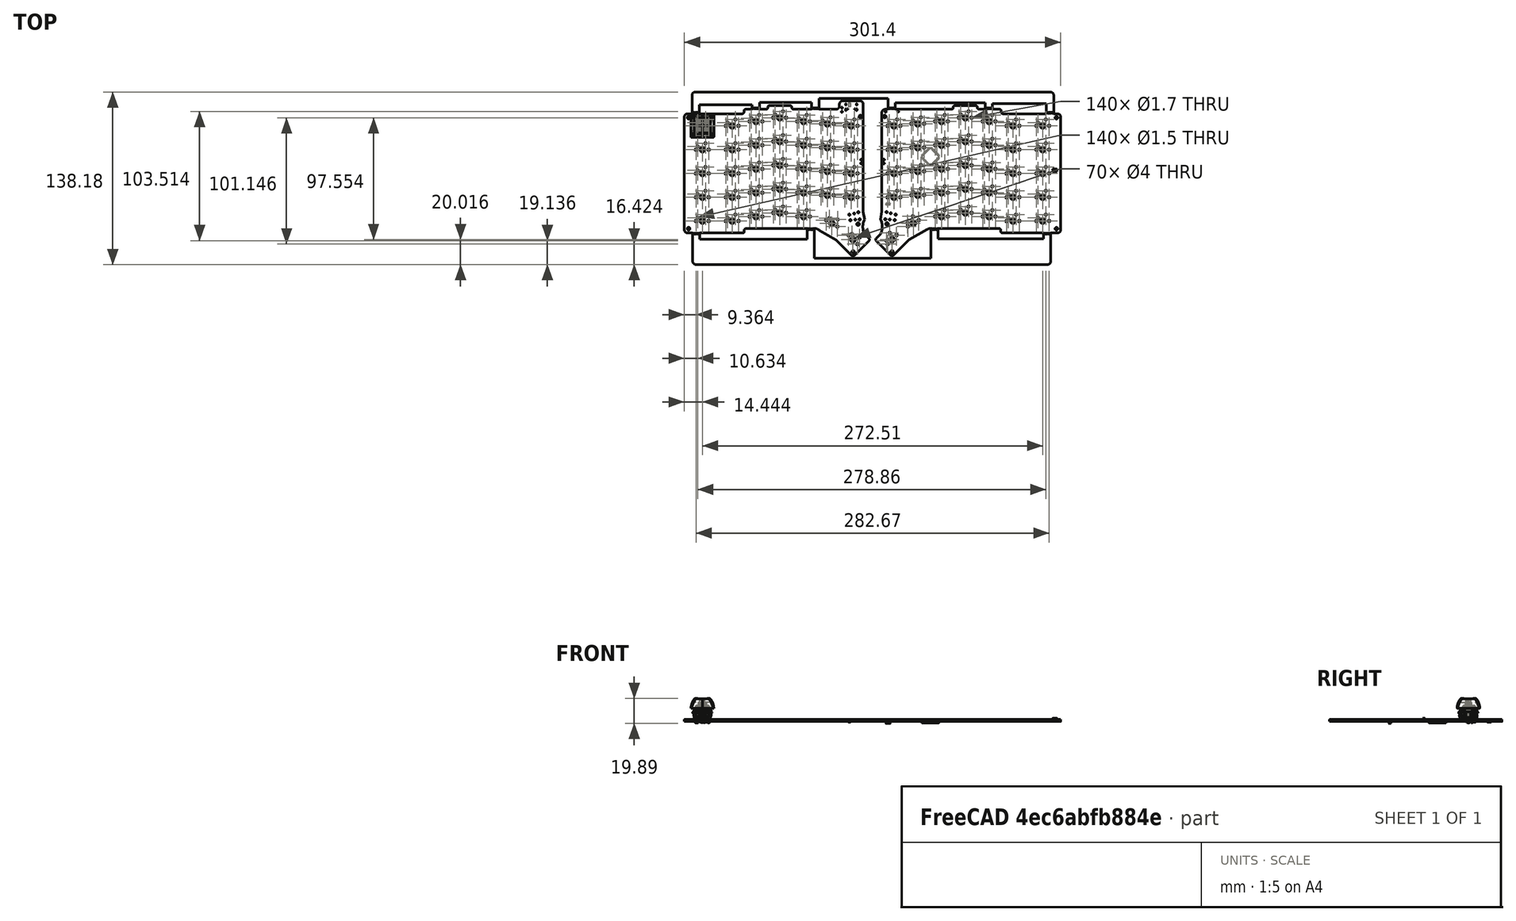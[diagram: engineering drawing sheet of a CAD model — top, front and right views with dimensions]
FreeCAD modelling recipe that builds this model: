
FCSTD DOCUMENT  (FreeCAD 0.19R24291 (Git))
Label: wholeModel
License: All rights reserved
LicenseURL: http://en.wikipedia.org/wiki/All_rights_reserved
objects: App::Link×226, Part::Feature×7, App::Part×5, PartDesign::CoordinateSystem×1, Sketcher::SketchObject×1
note: 9 computed .brp shape members not serialized (recipe doc carries the construction recipe); baked Part::Feature solids carry a one-line shape summary decoded from their .brp

FEATURE [PartDesign::CoordinateSystem] Local_CS_2136
  AttacherType = Attacher::AttachEngine3D
FEATURE [Part::Feature] Pcb_2136
  shape: bbox 301.4 x 138.2 x 1.6 mm, 613 faces (baked)
FEATURE [Sketcher::SketchObject] PCB_Sketch_2136
  FullyConstrained = false
  sketch-geometry (205):
    g0: LineSegment StartX=297.923 StartY=-40.503 StartZ=0 EndX=294.907 EndY=-40.503 EndZ=0
    g1: LineSegment StartX=240.043 StartY=-36.947 StartZ=0 EndX=235.058 EndY=-36.947 EndZ=0
    g2: LineSegment StartX=162.192 StartY=-36.947 StartZ=0 EndX=160.001 EndY=-36.947 EndZ=0
    g3: LineSegment StartX=53.48 StartY=-36.947 StartZ=0 EndX=48.2095 EndY=-36.947 EndZ=0
    g4: LineSegment StartX=5.347 StartY=-40.503 StartZ=0 EndX=1.8545 EndY=-40.503 EndZ=0
    g5: LineSegment StartX=292.621 StartY=-136.007 StartZ=0 EndX=297.923 EndY=-136.007 EndZ=0
    g6: LineSegment StartX=196.609 StartY=-132.451 StartZ=0 EndX=195.688 EndY=-132.449 EndZ=0
    g7: LineSegment StartX=103.264 StartY=-132.451 StartZ=0 EndX=104.217 EndY=-132.449 EndZ=0
    g8: LineSegment StartX=202.451 StartY=-140.579 StartZ=0 EndX=286.779 EndY=-140.579 EndZ=0
    g9: LineSegment StartX=292.621 StartY=-156.2 StartZ=0 EndX=292.62 EndY=-158.608 EndZ=0
    g10: LineSegment StartX=134.252 StartY=-156.2 StartZ=0 EndX=196.609 EndY=-156.2 EndZ=0
    g11: LineSegment StartX=292.621 StartY=-137.277 StartZ=0 EndX=292.621 EndY=-156.2 EndZ=0
    g12: LineSegment StartX=286.779 StartY=-137.277 StartZ=0 EndX=286.779 EndY=-140.579 EndZ=0
    g13: LineSegment StartX=202.451 StartY=-133.721 StartZ=0 EndX=202.451 EndY=-140.579 EndZ=0
    g14: LineSegment StartX=196.609 StartY=-133.721 StartZ=0 EndX=196.609 EndY=-156.2 EndZ=0
    g15: LineSegment StartX=97.422 StartY=-140.833 StartZ=0 EndX=11.57 EndY=-140.833 EndZ=0
    g16: LineSegment StartX=97.422 StartY=-133.721 StartZ=0 EndX=97.422 EndY=-140.833 EndZ=0
    g17: LineSegment StartX=103.264 StartY=-133.721 StartZ=0 EndX=103.264 EndY=-156.2 EndZ=0
    g18: LineSegment StartX=5.855 StartY=-156.2 StartZ=0 EndX=5.8574 EndY=-158.61 EndZ=0
    g19: LineSegment StartX=5.855 StartY=-137.277 StartZ=0 EndX=5.855 EndY=-156.2 EndZ=0
    g20: LineSegment StartX=11.57 StartY=-140.833 StartZ=0 EndX=11.57 EndY=-137.277 EndZ=0
    g21: LineSegment StartX=134.252 StartY=-156.2 StartZ=0 EndX=103.264 EndY=-156.2 EndZ=0
    g22: LineSegment StartX=289.953 StartY=-161.275 StartZ=0 EndX=8.5244 EndY=-161.277 EndZ=0
    g23: LineSegment StartX=294.904 StartY=-25.7686 StartZ=0 EndX=294.907 EndY=-28.184 EndZ=0
    g24: LineSegment StartX=108.217 StartY=-23.104 StartZ=0 EndX=292.237 EndY=-23.1016 EndZ=0
    g25: LineSegment StartX=294.907 StartY=-39.233 StartZ=0 EndX=294.907 EndY=-28.184 EndZ=0
    g26: LineSegment StartX=289.065 StartY=-32.502 StartZ=0 EndX=289.065 EndY=-39.233 EndZ=0
    g27: LineSegment StartX=245.885 StartY=-32.502 StartZ=0 EndX=289.065 EndY=-32.502 EndZ=0
    g28: LineSegment StartX=245.885 StartY=-35.677 StartZ=0 EndX=245.885 EndY=-32.502 EndZ=0
    g29: LineSegment StartX=240.043 StartY=-31.613 StartZ=0 EndX=240.043 EndY=-35.677 EndZ=0
    g30: LineSegment StartX=168.034 StartY=-31.613 StartZ=0 EndX=240.043 EndY=-31.613 EndZ=0
    g31: LineSegment StartX=168.034 StartY=-35.55 StartZ=0 EndX=168.034 EndY=-31.613 EndZ=0
    g32: LineSegment StartX=162.192 StartY=-28.184 StartZ=0 EndX=162.192 EndY=-35.677 EndZ=0
    g33: LineSegment StartX=126.505 StartY=-28.184 StartZ=0 EndX=162.192 EndY=-28.184 EndZ=0
    g34: LineSegment StartX=5.347 StartY=-25.771 StartZ=0 EndX=5.347 EndY=-28.184 EndZ=0
    g35: LineSegment StartX=106.947 StartY=-23.104 StartZ=0 EndX=8.014 EndY=-23.104 EndZ=0
    g36: LineSegment StartX=5.347 StartY=-28.311 StartZ=0 EndX=5.347 EndY=-28.184 EndZ=0
    g37: LineSegment StartX=5.347 StartY=-39.233 StartZ=0 EndX=5.347 EndY=-28.311 EndZ=0
    g38: LineSegment StartX=11.189 StartY=-33.391 StartZ=0 EndX=11.189 EndY=-39.233 EndZ=0
    g39: LineSegment StartX=53.48 StartY=-33.391 StartZ=0 EndX=11.189 EndY=-33.391 EndZ=0
    g40: LineSegment StartX=53.48 StartY=-35.677 StartZ=0 EndX=53.48 EndY=-33.391 EndZ=0
    g41: LineSegment StartX=59.322 StartY=-31.486 StartZ=0 EndX=59.322 EndY=-35.677 EndZ=0
    g42: LineSegment StartX=101.105 StartY=-31.486 StartZ=0 EndX=59.322 EndY=-31.486 EndZ=0
    g43: LineSegment StartX=101.105 StartY=-35.677 StartZ=0 EndX=101.105 EndY=-31.486 EndZ=0
    g44: LineSegment StartX=106.947 StartY=-23.104 StartZ=0 EndX=108.217 EndY=-23.104 EndZ=0
    g45: LineSegment StartX=106.947 StartY=-28.184 StartZ=0 EndX=126.505 EndY=-28.184 EndZ=0
    g46: LineSegment StartX=106.947 StartY=-35.677 StartZ=0 EndX=106.947 EndY=-28.184 EndZ=0
    g47: LineSegment StartX=5.347 StartY=-39.233 StartZ=0 EndX=5.347 EndY=-40.503 EndZ=0
    g48: LineSegment StartX=11.189 StartY=-39.233 StartZ=0 EndX=11.189 EndY=-40.503 EndZ=0
    g49: LineSegment StartX=53.48 StartY=-35.677 StartZ=0 EndX=53.48 EndY=-36.947 EndZ=0
    g50: LineSegment StartX=59.322 StartY=-35.677 StartZ=0 EndX=59.322 EndY=-36.947 EndZ=0
    g51: LineSegment StartX=101.105 StartY=-35.677 StartZ=0 EndX=101.105 EndY=-36.947 EndZ=0
    g52: LineSegment StartX=106.947 StartY=-35.677 StartZ=0 EndX=106.947 EndY=-36.947 EndZ=0
    g53: LineSegment StartX=162.192 StartY=-35.677 StartZ=0 EndX=162.192 EndY=-36.947 EndZ=0
    g54: LineSegment StartX=168.034 StartY=-35.55 StartZ=0 EndX=168.034 EndY=-36.947 EndZ=0
    g55: LineSegment StartX=240.043 StartY=-35.677 StartZ=0 EndX=240.043 EndY=-36.947 EndZ=0
    g56: LineSegment StartX=245.885 StartY=-35.677 StartZ=0 EndX=245.885 EndY=-36.947 EndZ=0
    g57: LineSegment StartX=289.065 StartY=-39.233 StartZ=0 EndX=289.065 EndY=-40.503 EndZ=0
    g58: LineSegment StartX=294.907 StartY=-39.233 StartZ=0 EndX=294.907 EndY=-40.503 EndZ=0
    g59: LineSegment StartX=286.779 StartY=-136.007 StartZ=0 EndX=286.779 EndY=-137.277 EndZ=0
    g60: LineSegment StartX=292.621 StartY=-136.007 StartZ=0 EndX=292.621 EndY=-137.277 EndZ=0
    g61: LineSegment StartX=196.609 StartY=-132.451 StartZ=0 EndX=196.609 EndY=-133.721 EndZ=0
    g62: LineSegment StartX=202.451 StartY=-132.451 StartZ=0 EndX=202.451 EndY=-133.721 EndZ=0
    g63: LineSegment StartX=97.422 StartY=-132.451 StartZ=0 EndX=97.422 EndY=-133.721 EndZ=0
    g64: LineSegment StartX=103.264 StartY=-132.451 StartZ=0 EndX=103.264 EndY=-133.721 EndZ=0
    g65: LineSegment StartX=11.57 StartY=-136.007 StartZ=0 EndX=11.57 EndY=-137.277 EndZ=0
    g66: LineSegment StartX=11.57 StartY=-136.007 StartZ=0 EndX=45.9235 EndY=-136.007 EndZ=0
    g67: LineSegment StartX=5.855 StartY=-136.007 StartZ=0 EndX=5.855 EndY=-137.277 EndZ=0
    g68: LineSegment StartX=1.8545 StartY=-136.007 StartZ=0 EndX=5.855 EndY=-136.007 EndZ=0
    g69: LineSegment StartX=193.656 StartY=-133.086 StartZ=0 EndX=179.178 EndY=-141.341 EndZ=0
    g70: LineSegment StartX=214.484 StartY=-35.677 StartZ=0 EndX=214.484 EndY=-35.296 EndZ=0
    g71: LineSegment StartX=147.016 StartY=-140.198 StartZ=0 EndX=143.587 EndY=-136.769 EndZ=0
    g72: LineSegment StartX=120.6 StartY=-141.468 StartZ=0 EndX=133.173 EndY=-154.041 EndZ=0
    g73: LineSegment StartX=106.249 StartY=-133.086 StartZ=0 EndX=106.629 EndY=-133.34 EndZ=0
    g74: LineSegment StartX=107.519 StartY=-133.848 StartZ=0 EndX=120.6 EndY=-141.468 EndZ=0
    g75: LineSegment StartX=107.519 StartY=-133.848 StartZ=0 EndX=106.629 EndY=-133.34 EndZ=0
    g76: LineSegment StartX=120.727 StartY=-36.947 StartZ=0 EndX=106.947 EndY=-36.947 EndZ=0
    g77: LineSegment StartX=123.394 StartY=-34.28 StartZ=0 EndX=123.394 EndY=-32.893 EndZ=0
    g78: LineSegment StartX=139.776 StartY=-30.216 StartZ=0 EndX=126.061 EndY=-30.216 EndZ=0
    g79: LineSegment StartX=142.444 StartY=-38.725 StartZ=0 EndX=142.443 EndY=-32.893 EndZ=0
    g80: LineSegment StartX=85.2935 StartY=-35.677 StartZ=0 EndX=85.2935 EndY=-35.296 EndZ=0
    g81: LineSegment StartX=101.105 StartY=-36.947 StartZ=0 EndX=86.5635 EndY=-36.947 EndZ=0
    g82: LineSegment StartX=84.0235 StartY=-34.026 StartZ=0 EndX=67.2595 EndY=-34.026 EndZ=0
    g83: LineSegment StartX=65.9895 StartY=-35.296 StartZ=0 EndX=65.9895 EndY=-35.677 EndZ=0
    g84: LineSegment StartX=152.762 StartY=-140.198 StartZ=0 EndX=156.191 EndY=-136.769 EndZ=0
    g85: LineSegment StartX=164.446 StartY=-153.914 StartZ=0 EndX=152.762 EndY=-142.23 EndZ=0
    g86: LineSegment StartX=178.924 StartY=-141.468 StartZ=0 EndX=166.478 EndY=-153.914 EndZ=0
    g87: LineSegment StartX=179.178 StartY=-141.341 StartZ=0 EndX=178.924 EndY=-141.468 EndZ=0
    g88: LineSegment StartX=214.738 StartY=-132.451 StartZ=0 EndX=202.451 EndY=-132.451 EndZ=0
    g89: LineSegment StartX=233.534 StartY=-132.451 StartZ=0 EndX=214.738 EndY=-132.451 EndZ=0
    g90: LineSegment StartX=251.314 StartY=-132.451 StartZ=0 EndX=233.534 EndY=-132.451 EndZ=0
    g91: LineSegment StartX=252.584 StartY=-134.737 StartZ=0 EndX=252.584 EndY=-133.721 EndZ=0
    g92: LineSegment StartX=286.779 StartY=-136.007 StartZ=0 EndX=253.854 EndY=-136.007 EndZ=0
    g93: LineSegment StartX=300.59 StartY=-43.17 StartZ=0 EndX=300.59 EndY=-133.34 EndZ=0
    g94: LineSegment StartX=254.108 StartY=-40.503 StartZ=0 EndX=289.065 EndY=-40.503 EndZ=0
    g95: LineSegment StartX=252.838 StartY=-38.217 StartZ=0 EndX=252.838 EndY=-39.233 EndZ=0
    g96: LineSegment StartX=245.885 StartY=-36.947 StartZ=0 EndX=251.568 EndY=-36.947 EndZ=0
    g97: LineSegment StartX=233.788 StartY=-35.296 StartZ=0 EndX=233.788 EndY=-35.677 EndZ=0
    g98: LineSegment StartX=157.334 StartY=-39.614 StartZ=0 EndX=157.334 EndY=-40.503 EndZ=0
    g99: LineSegment StartX=213.214 StartY=-36.947 StartZ=0 EndX=168.034 EndY=-36.947 EndZ=0
    g100: LineSegment StartX=232.518 StartY=-34.026 StartZ=0 EndX=215.754 EndY=-34.026 EndZ=0
    g101: LineSegment StartX=157.334 StartY=-116.068 StartZ=0 EndX=157.334 EndY=-40.503 EndZ=0
    g102: LineSegment StartX=157.334 StartY=-118.862 StartZ=0 EndX=156.191 EndY=-125.085 EndZ=0
    g103: LineSegment StartX=157.334 StartY=-116.957 StartZ=0 EndX=157.334 EndY=-118.862 EndZ=0
    g104: LineSegment StartX=157.334 StartY=-116.068 StartZ=0 EndX=157.334 EndY=-116.957 EndZ=0
    g105: LineSegment StartX=142.444 StartY=-116.195 StartZ=0 EndX=142.444 EndY=-41.138 EndZ=0
    g106: LineSegment StartX=142.444 StartY=-118.989 StartZ=0 EndX=143.587 EndY=-125.085 EndZ=0
    g107: LineSegment StartX=142.444 StartY=-116.957 StartZ=0 EndX=142.444 EndY=-118.989 EndZ=0
    g108: LineSegment StartX=142.444 StartY=-116.195 StartZ=0 EndX=142.444 EndY=-116.957 EndZ=0
    g109: LineSegment StartX=135.204 StartY=-154.041 StartZ=0 EndX=147.016 EndY=-142.23 EndZ=0
    g110: LineSegment StartX=85.0395 StartY=-132.451 StartZ=0 EndX=97.422 EndY=-132.451 EndZ=0
    g111: LineSegment StartX=66.2435 StartY=-132.451 StartZ=0 EndX=85.0395 EndY=-132.451 EndZ=0
    g112: LineSegment StartX=48.4635 StartY=-132.451 StartZ=0 EndX=66.2435 EndY=-132.451 EndZ=0
    g113: LineSegment StartX=47.1935 StartY=-134.737 StartZ=0 EndX=47.1935 EndY=-133.721 EndZ=0
    g114: LineSegment StartX=-0.8125 StartY=-43.17 StartZ=0 EndX=-0.8125 EndY=-133.34 EndZ=0
    g115: LineSegment StartX=45.6695 StartY=-40.503 StartZ=0 EndX=11.189 EndY=-40.503 EndZ=0
    g116: LineSegment StartX=46.9395 StartY=-38.217 StartZ=0 EndX=46.9395 EndY=-39.233 EndZ=0
    g117: LineSegment StartX=64.7195 StartY=-36.947 StartZ=0 EndX=59.322 EndY=-36.947 EndZ=0
    g118: LineSegment StartX=142.444 StartY=-41.138 StartZ=0 EndX=142.444 EndY=-38.725 EndZ=0
    g119: ArcOfCircle CenterX=289.953 CenterY=-158.608 CenterZ=0 NormalX=0 NormalY=0 NormalZ=1 AngleXU=0 Radius=2.667 StartAngle=4.71239 EndAngle=6.28319
    g120: ArcOfCircle CenterX=8.5244 CenterY=-158.61 CenterZ=0 NormalX=0 NormalY=0 NormalZ=1 AngleXU=0 Radius=2.667 StartAngle=3.14159 EndAngle=4.71239
    g121: ArcOfCircle CenterX=292.237 CenterY=-25.7686 CenterZ=0 NormalX=0 NormalY=0 NormalZ=1 AngleXU=0 Radius=2.667 StartAngle=0 EndAngle=1.5708
    g122: ArcOfCircle CenterX=8.014 CenterY=-25.771 CenterZ=0 NormalX=0 NormalY=0 NormalZ=1 AngleXU=0 Radius=2.667 StartAngle=1.5708 EndAngle=3.14159
    g123: ArcOfCircle CenterX=154.254 CenterY=-130.927 CenterZ=0 NormalX=0 NormalY=0 NormalZ=1 AngleXU=0 Radius=12.1629 StartAngle=2.64058 EndAngle=3.64261
    g124: ArcOfCircle CenterX=145.523 CenterY=-130.927 CenterZ=0 NormalX=0 NormalY=0 NormalZ=1 AngleXU=0 Radius=12.1629 StartAngle=5.78217 EndAngle=6.7842
    g125: ArcOfCircle CenterX=195.688 CenterY=-136.007 CenterZ=0 NormalX=0 NormalY=0 NormalZ=1 AngleXU=0 Radius=3.55827 StartAngle=1.5708 EndAngle=2.1786
    g126: ArcOfCircle CenterX=153.778 CenterY=-141.214 CenterZ=0 NormalX=0 NormalY=0 NormalZ=1 AngleXU=0 Radius=1.43684 StartAngle=2.35619 EndAngle=3.92699
    g127: ArcOfCircle CenterX=297.923 CenterY=-43.17 CenterZ=0 NormalX=0 NormalY=0 NormalZ=1 AngleXU=0 Radius=2.667 StartAngle=0 EndAngle=1.5708
    g128: ArcOfCircle CenterX=297.923 CenterY=-133.34 CenterZ=0 NormalX=0 NormalY=0 NormalZ=1 AngleXU=0 Radius=2.667 StartAngle=4.71239 EndAngle=6.28319
    g129: ArcOfCircle CenterX=251.314 CenterY=-133.721 CenterZ=0 NormalX=0 NormalY=0 NormalZ=1 AngleXU=0 Radius=1.27 StartAngle=0 EndAngle=1.5708
    g130: ArcOfCircle CenterX=253.854 CenterY=-134.737 CenterZ=0 NormalX=0 NormalY=0 NormalZ=1 AngleXU=0 Radius=1.27 StartAngle=3.14159 EndAngle=4.71239
    g131: ArcOfCircle CenterX=254.108 CenterY=-39.233 CenterZ=0 NormalX=0 NormalY=0 NormalZ=1 AngleXU=0 Radius=1.27 StartAngle=3.14159 EndAngle=4.71239
    g132: ArcOfCircle CenterX=251.568 CenterY=-38.217 CenterZ=0 NormalX=0 NormalY=0 NormalZ=1 AngleXU=0 Radius=1.27 StartAngle=0 EndAngle=1.5708
    g133: ArcOfCircle CenterX=235.058 CenterY=-35.677 CenterZ=0 NormalX=0 NormalY=0 NormalZ=1 AngleXU=0 Radius=1.27 StartAngle=3.14159 EndAngle=4.71239
    g134: ArcOfCircle CenterX=232.518 CenterY=-35.296 CenterZ=0 NormalX=0 NormalY=0 NormalZ=1 AngleXU=0 Radius=1.27 StartAngle=0 EndAngle=1.5708
    g135: ArcOfCircle CenterX=215.754 CenterY=-35.296 CenterZ=0 NormalX=0 NormalY=0 NormalZ=1 AngleXU=0 Radius=1.27 StartAngle=1.5708 EndAngle=3.14159
    g136: ArcOfCircle CenterX=213.214 CenterY=-35.677 CenterZ=0 NormalX=0 NormalY=0 NormalZ=1 AngleXU=0 Radius=1.27 StartAngle=4.71239 EndAngle=6.28319
    g137: ArcOfCircle CenterX=146 CenterY=-141.214 CenterZ=0 NormalX=0 NormalY=0 NormalZ=1 AngleXU=0 Radius=1.43684 StartAngle=5.49779 EndAngle=7.06858
    g138: ArcOfCircle CenterX=165.462 CenterY=-152.898 CenterZ=0 NormalX=0 NormalY=0 NormalZ=1 AngleXU=0 Radius=1.43684 StartAngle=3.92699 EndAngle=5.49779
    g139: ArcOfCircle CenterX=134.189 CenterY=-153.025 CenterZ=0 NormalX=0 NormalY=0 NormalZ=1 AngleXU=0 Radius=1.43684 StartAngle=3.92699 EndAngle=5.49779
    g140: ArcOfCircle CenterX=104.217 CenterY=-136.007 CenterZ=0 NormalX=0 NormalY=0 NormalZ=1 AngleXU=0 Radius=3.55827 StartAngle=0.962994 EndAngle=1.5708
    g141: ArcOfCircle CenterX=1.8545 CenterY=-133.34 CenterZ=0 NormalX=0 NormalY=0 NormalZ=1 AngleXU=0 Radius=2.667 StartAngle=3.14159 EndAngle=4.71239
    g142: ArcOfCircle CenterX=1.8545 CenterY=-43.17 CenterZ=0 NormalX=0 NormalY=0 NormalZ=1 AngleXU=0 Radius=2.667 StartAngle=1.5708 EndAngle=3.14159
    g143: ArcOfCircle CenterX=48.4635 CenterY=-133.721 CenterZ=0 NormalX=0 NormalY=0 NormalZ=1 AngleXU=0 Radius=1.27 StartAngle=1.5708 EndAngle=3.14159
    g144: ArcOfCircle CenterX=45.9235 CenterY=-134.737 CenterZ=0 NormalX=0 NormalY=0 NormalZ=1 AngleXU=0 Radius=1.27 StartAngle=4.71239 EndAngle=6.28319
    g145: ArcOfCircle CenterX=45.6695 CenterY=-39.233 CenterZ=0 NormalX=0 NormalY=0 NormalZ=1 AngleXU=0 Radius=1.27 StartAngle=4.71239 EndAngle=6.28319
    g146: ArcOfCircle CenterX=48.2095 CenterY=-38.217 CenterZ=0 NormalX=0 NormalY=0 NormalZ=1 AngleXU=0 Radius=1.27 StartAngle=1.5708 EndAngle=3.14159
    g147: ArcOfCircle CenterX=64.7195 CenterY=-35.677 CenterZ=0 NormalX=0 NormalY=0 NormalZ=1 AngleXU=0 Radius=1.27 StartAngle=4.71239 EndAngle=6.28319
    g148: ArcOfCircle CenterX=86.5635 CenterY=-35.677 CenterZ=0 NormalX=0 NormalY=0 NormalZ=1 AngleXU=0 Radius=1.27 StartAngle=3.14159 EndAngle=4.71239
    g149: ArcOfCircle CenterX=67.2595 CenterY=-35.296 CenterZ=0 NormalX=0 NormalY=0 NormalZ=1 AngleXU=0 Radius=1.27 StartAngle=1.5708 EndAngle=3.14159
    g150: ArcOfCircle CenterX=84.0235 CenterY=-35.296 CenterZ=0 NormalX=0 NormalY=0 NormalZ=1 AngleXU=0 Radius=1.27 StartAngle=0 EndAngle=1.5708
    g151: ArcOfCircle CenterX=120.727 CenterY=-34.28 CenterZ=0 NormalX=0 NormalY=0 NormalZ=1 AngleXU=0 Radius=2.667 StartAngle=4.71239 EndAngle=6.28319
    g152: ArcOfCircle CenterX=160.001 CenterY=-39.614 CenterZ=0 NormalX=0 NormalY=0 NormalZ=1 AngleXU=0 Radius=2.667 StartAngle=1.5708 EndAngle=3.14159
    g153: ArcOfCircle CenterX=126.06 CenterY=-32.883 CenterZ=0 NormalX=0 NormalY=0 NormalZ=1 AngleXU=0 Radius=2.66702 StartAngle=1.5708 EndAngle=3.14534
    g154: ArcOfCircle CenterX=139.776 CenterY=-32.883 CenterZ=0 NormalX=0 NormalY=0 NormalZ=1 AngleXU=0 Radius=2.66702 StartAngle=6.27944 EndAngle=7.85398
    g155: Circle CenterX=10.554 CenterY=-39.741 CenterZ=0 NormalX=0 NormalY=0 NormalZ=1 AngleXU=0 Radius=0.457905
    g156: Circle CenterX=5.982 CenterY=-39.741 CenterZ=0 NormalX=0 NormalY=0 NormalZ=1 AngleXU=0 Radius=0.457905
    g157: Circle CenterX=9.411 CenterY=-39.741 CenterZ=0 NormalX=0 NormalY=0 NormalZ=1 AngleXU=0 Radius=0.457905
    g158: Circle CenterX=7.125 CenterY=-39.741 CenterZ=0 NormalX=0 NormalY=0 NormalZ=1 AngleXU=0 Radius=0.457905
    g159: Circle CenterX=8.268 CenterY=-39.741 CenterZ=0 NormalX=0 NormalY=0 NormalZ=1 AngleXU=0 Radius=0.457905
    g160: Circle CenterX=58.687 CenterY=-36.185 CenterZ=0 NormalX=0 NormalY=0 NormalZ=1 AngleXU=0 Radius=0.457905
    g161: Circle CenterX=54.115 CenterY=-36.185 CenterZ=0 NormalX=0 NormalY=0 NormalZ=1 AngleXU=0 Radius=0.457905
    g162: Circle CenterX=57.544 CenterY=-36.185 CenterZ=0 NormalX=0 NormalY=0 NormalZ=1 AngleXU=0 Radius=0.457905
    g163: Circle CenterX=55.258 CenterY=-36.185 CenterZ=0 NormalX=0 NormalY=0 NormalZ=1 AngleXU=0 Radius=0.457905
    g164: Circle CenterX=56.401 CenterY=-36.185 CenterZ=0 NormalX=0 NormalY=0 NormalZ=1 AngleXU=0 Radius=0.457905
    g165: Circle CenterX=106.312 CenterY=-36.185 CenterZ=0 NormalX=0 NormalY=0 NormalZ=1 AngleXU=0 Radius=0.457905
    g166: Circle CenterX=101.74 CenterY=-36.185 CenterZ=0 NormalX=0 NormalY=0 NormalZ=1 AngleXU=0 Radius=0.457905
    g167: Circle CenterX=105.169 CenterY=-36.185 CenterZ=0 NormalX=0 NormalY=0 NormalZ=1 AngleXU=0 Radius=0.457905
    g168: Circle CenterX=102.883 CenterY=-36.185 CenterZ=0 NormalX=0 NormalY=0 NormalZ=1 AngleXU=0 Radius=0.457905
    g169: Circle CenterX=104.026 CenterY=-36.185 CenterZ=0 NormalX=0 NormalY=0 NormalZ=1 AngleXU=0 Radius=0.457905
    g170: Circle CenterX=167.399 CenterY=-36.185 CenterZ=0 NormalX=0 NormalY=0 NormalZ=1 AngleXU=0 Radius=0.457905
    g171: Circle CenterX=162.827 CenterY=-36.185 CenterZ=0 NormalX=0 NormalY=0 NormalZ=1 AngleXU=0 Radius=0.457905
    g172: Circle CenterX=166.256 CenterY=-36.185 CenterZ=0 NormalX=0 NormalY=0 NormalZ=1 AngleXU=0 Radius=0.457905
    g173: Circle CenterX=163.97 CenterY=-36.185 CenterZ=0 NormalX=0 NormalY=0 NormalZ=1 AngleXU=0 Radius=0.457905
    g174: Circle CenterX=165.113 CenterY=-36.185 CenterZ=0 NormalX=0 NormalY=0 NormalZ=1 AngleXU=0 Radius=0.457905
    g175: Circle CenterX=245.25 CenterY=-36.185 CenterZ=0 NormalX=0 NormalY=0 NormalZ=1 AngleXU=0 Radius=0.457905
    g176: Circle CenterX=240.678 CenterY=-36.185 CenterZ=0 NormalX=0 NormalY=0 NormalZ=1 AngleXU=0 Radius=0.457905
    g177: Circle CenterX=244.107 CenterY=-36.185 CenterZ=0 NormalX=0 NormalY=0 NormalZ=1 AngleXU=0 Radius=0.457905
    g178: Circle CenterX=241.821 CenterY=-36.185 CenterZ=0 NormalX=0 NormalY=0 NormalZ=1 AngleXU=0 Radius=0.457905
    g179: Circle CenterX=242.964 CenterY=-36.185 CenterZ=0 NormalX=0 NormalY=0 NormalZ=1 AngleXU=0 Radius=0.457905
    g180: Circle CenterX=294.272 CenterY=-39.741 CenterZ=0 NormalX=0 NormalY=0 NormalZ=1 AngleXU=0 Radius=0.457905
    g181: Circle CenterX=289.7 CenterY=-39.741 CenterZ=0 NormalX=0 NormalY=0 NormalZ=1 AngleXU=0 Radius=0.457905
    g182: Circle CenterX=293.129 CenterY=-39.741 CenterZ=0 NormalX=0 NormalY=0 NormalZ=1 AngleXU=0 Radius=0.457905
    g183: Circle CenterX=290.843 CenterY=-39.741 CenterZ=0 NormalX=0 NormalY=0 NormalZ=1 AngleXU=0 Radius=0.457905
    g184: Circle CenterX=291.986 CenterY=-39.741 CenterZ=0 NormalX=0 NormalY=0 NormalZ=1 AngleXU=0 Radius=0.457905
    g185: Circle CenterX=291.986 CenterY=-136.515 CenterZ=0 NormalX=0 NormalY=0 NormalZ=1 AngleXU=0 Radius=0.457905
    g186: Circle CenterX=287.414 CenterY=-136.515 CenterZ=0 NormalX=0 NormalY=0 NormalZ=1 AngleXU=0 Radius=0.457905
    g187: Circle CenterX=290.843 CenterY=-136.515 CenterZ=0 NormalX=0 NormalY=0 NormalZ=1 AngleXU=0 Radius=0.457905
    g188: Circle CenterX=288.557 CenterY=-136.515 CenterZ=0 NormalX=0 NormalY=0 NormalZ=1 AngleXU=0 Radius=0.457905
    g189: Circle CenterX=289.7 CenterY=-136.515 CenterZ=0 NormalX=0 NormalY=0 NormalZ=1 AngleXU=0 Radius=0.457905
    g190: Circle CenterX=201.816 CenterY=-132.959 CenterZ=0 NormalX=0 NormalY=0 NormalZ=1 AngleXU=0 Radius=0.457905
    g191: Circle CenterX=197.244 CenterY=-132.959 CenterZ=0 NormalX=0 NormalY=0 NormalZ=1 AngleXU=0 Radius=0.457905
    g192: Circle CenterX=200.673 CenterY=-132.959 CenterZ=0 NormalX=0 NormalY=0 NormalZ=1 AngleXU=0 Radius=0.457905
    g193: Circle CenterX=198.387 CenterY=-132.959 CenterZ=0 NormalX=0 NormalY=0 NormalZ=1 AngleXU=0 Radius=0.457905
    g194: Circle CenterX=199.53 CenterY=-132.959 CenterZ=0 NormalX=0 NormalY=0 NormalZ=1 AngleXU=0 Radius=0.457905
    g195: Circle CenterX=102.629 CenterY=-132.959 CenterZ=0 NormalX=0 NormalY=0 NormalZ=1 AngleXU=0 Radius=0.457905
    g196: Circle CenterX=98.057 CenterY=-132.959 CenterZ=0 NormalX=0 NormalY=0 NormalZ=1 AngleXU=0 Radius=0.457905
    g197: Circle CenterX=101.486 CenterY=-132.959 CenterZ=0 NormalX=0 NormalY=0 NormalZ=1 AngleXU=0 Radius=0.457905
    g198: Circle CenterX=99.2 CenterY=-132.959 CenterZ=0 NormalX=0 NormalY=0 NormalZ=1 AngleXU=0 Radius=0.457905
    g199: Circle CenterX=100.343 CenterY=-132.959 CenterZ=0 NormalX=0 NormalY=0 NormalZ=1 AngleXU=0 Radius=0.457905
    g200: Circle CenterX=6.43991 CenterY=-136.515 CenterZ=0 NormalX=0 NormalY=0 NormalZ=1 AngleXU=0 Radius=0.457905
    g201: Circle CenterX=11.0119 CenterY=-136.515 CenterZ=0 NormalX=0 NormalY=0 NormalZ=1 AngleXU=0 Radius=0.457905
    g202: Circle CenterX=8.7259 CenterY=-136.515 CenterZ=0 NormalX=0 NormalY=0 NormalZ=1 AngleXU=0 Radius=0.457905
    g203: Circle CenterX=9.8689 CenterY=-136.515 CenterZ=0 NormalX=0 NormalY=0 NormalZ=1 AngleXU=0 Radius=0.457905
    g204: Circle CenterX=7.58291 CenterY=-136.515 CenterZ=0 NormalX=0 NormalY=0 NormalZ=1 AngleXU=0 Radius=0.457905
  constraints (155):
    c: Coincident(g141,g114)
    c: Coincident(g114,g142)
    c: Coincident(g141,g68)
    c: Coincident(g142,g4)
    c: Coincident(g47,g4)
    c: Coincident(g37,g47)
    c: Coincident(g37,g36)
    c: Coincident(g34,g36)
    c: Coincident(g122,g34)
    c: Coincident(g120,g18)
    c: Coincident(g18,g19)
    c: Coincident(g67,g19)
    c: Coincident(g68,g67)
    c: Coincident(g122,g35)
    c: Coincident(g120,g22)
    c: Coincident(g115,g48)
    c: Coincident(g38,g48)
    c: Coincident(g39,g38)
    c: Coincident(g15,g20)
    c: Coincident(g65,g20)
    c: Coincident(g65,g66)
    c: Coincident(g115,g145)
    c: Coincident(g66,g144)
    c: Coincident(g116,g145)
    c: Coincident(g116,g146)
    c: Coincident(g144,g113)
    c: Coincident(g113,g143)
    c: Coincident(g146,g3)
    c: Coincident(g143,g112)
    c: Coincident(g3,g49)
    c: Coincident(g49,g40)
    c: Coincident(g39,g40)
    c: Coincident(g50,g117)
    c: Coincident(g50,g41)
    c: Coincident(g41,g42)
    c: Coincident(g147,g117)
    c: Coincident(g147,g83)
    c: Coincident(g149,g83)
    c: Coincident(g111,g112)
    c: Coincident(g149,g82)
    c: Coincident(g82,g150)
    c: Coincident(g110,g111)
    c: Coincident(g80,g148)
    c: Coincident(g80,g150)
    c: Coincident(g81,g148)
    c: Coincident(g15,g16)
    c: Coincident(g63,g16)
    c: Coincident(g63,g110)
    c: Coincident(g81,g51)
    c: Coincident(g43,g51)
    c: Coincident(g42,g43)
    c: Coincident(g21,g17)
    c: Coincident(g64,g17)
    c: Coincident(g7,g64)
    c: Coincident(g7,g140)
    c: Coincident(g73,g140)
    c: Coincident(g75,g73)
    c: Coincident(g76,g52)
    c: Coincident(g52,g46)
    c: Coincident(g46,g45)
    c: Coincident(g35,g44)
    c: Coincident(g75,g74)
    c: Coincident(g44,g24)
    c: Coincident(g74,g72)
    c: Coincident(g76,g151)
    c: Coincident(g77,g151)
    c: Coincident(g77,g153)
    c: Coincident(g153,g78)
    c: Coincident(g45,g33)
    c: Coincident(g72,g139)
    c: Coincident(g21,g10)
    c: Coincident(g109,g139)
    c: Coincident(g78,g154)
    c: Coincident(g107,g106)
    c: Coincident(g107,g108)
    c: Coincident(g108,g105)
    c: Coincident(g118,g105)
    c: Coincident(g79,g118)
    c: Coincident(g79,g154)
    c: Coincident(g123,g71)
    c: Coincident(g106,g123)
    c: Coincident(g137,g109)
    c: Coincident(g71,g137)
    c: Coincident(g85,g126)
    c: Coincident(g84,g126)
    c: Coincident(g124,g84)
    c: Coincident(g102,g124)
    c: Coincident(g103,g102)
    c: Coincident(g104,g103)
    c: Coincident(g104,g101)
    c: Coincident(g98,g101)
    c: Coincident(g98,g152)
    c: Coincident(g2,g152)
    c: Coincident(g2,g53)
    c: Coincident(g32,g53)
    c: Coincident(g32,g33)
    c: Coincident(g85,g138)
    c: Coincident(g86,g138)
    c: Coincident(g54,g99)
    c: Coincident(g54,g31)
    c: Coincident(g30,g31)
    c: Coincident(g87,g86)
    c: Coincident(g87,g69)
    c: Coincident(g69,g125)
    c: Coincident(g6,g125)
    c: Coincident(g14,g10)
    c: Coincident(g61,g14)
    c: Coincident(g6,g61)
    c: Coincident(g8,g13)
    c: Coincident(g62,g13)
    c: Coincident(g62,g88)
    c: Coincident(g136,g99)
    c: Coincident(g70,g136)
    c: Coincident(g70,g135)
    c: Coincident(g88,g89)
    c: Coincident(g100,g135)
    c: Coincident(g134,g100)
    c: Coincident(g90,g89)
    c: Coincident(g133,g97)
    c: Coincident(g97,g134)
    c: Coincident(g1,g133)
    c: Coincident(g55,g1)
    c: Coincident(g55,g29)
    c: Coincident(g29,g30)
    c: Coincident(g56,g96)
    c: Coincident(g28,g56)
    c: Coincident(g27,g28)
    c: Coincident(g129,g90)
    c: Coincident(g132,g96)
    c: Coincident(g130,g91)
    c: Coincident(g129,g91)
    c: Coincident(g131,g95)
    c: Coincident(g132,g95)
    c: Coincident(g130,g92)
    c: Coincident(g94,g131)
    c: Coincident(g8,g12)
    c: Coincident(g59,g12)
    c: Coincident(g59,g92)
    c: Coincident(g94,g57)
    c: Coincident(g26,g57)
    c: Coincident(g26,g27)
    c: Coincident(g22,g119)
    c: Coincident(g121,g24)
    c: Coincident(g9,g119)
    c: Coincident(g11,g9)
    c: Coincident(g11,g60)
    c: Coincident(g5,g60)
    c: Coincident(g0,g58)
    c: Coincident(g25,g58)
    c: Coincident(g23,g25)
    c: Coincident(g23,g121)
    c: Coincident(g128,g5)
    c: Coincident(g0,g127)
    c: Coincident(g128,g93)
    c: Coincident(g93,g127)
FEATURE [App::Part] Board_Geoms_2136
  Group = -> [Local_CS_2136,Pcb_2136,PCB_Sketch_2136]
  Origin = -> Origin
FEATURE [Part::Feature] Shape  label="SW1_SW_Cherry_MX_PCB_cp_61322BA2[2]"
  Placement = pos=(13.6737,-50.1067,0) rot=(0,0,1;0rad)
  shape: bbox 15.61 x 15.61 x 18.61 mm, 942 faces, 7 solids (baked)
FEATURE [Part::Feature] Shape001  label="SW1_Keycap_adjusted v39_61322BA2[3]"
  Placement = pos=(13.6737,-50.1067,9) rot=(1,0,0;1.5708rad)
  shape: bbox 18.32 x 18.3 x 7.723 mm, 77 faces (baked)
FEATURE [App::Link] SW1_SW_Cherry_MX_PCB_cp_61322BA2_2__ln_  label="SW2_SW_Cherry_MX_PCB_cp_61322B0C[2]"
  LinkPlacement = pos=(13.6737,-69.1568,0) rot=(0,0,1;0rad)
  LinkedObject = -> Shape
  Placement = pos=(13.6737,-69.1568,0) rot=(0,0,1;0rad)
FEATURE [App::Link] SW1_Keycap_adjusted_v39_61322BA2_3__ln_  label="SW2_Keycap_adjusted v39_61322B0C[3]"
  LinkPlacement = pos=(13.6737,-69.1568,9) rot=(1,0,0;1.5708rad)
  LinkedObject = -> Shape001
  Placement = pos=(13.6737,-69.1568,9) rot=(1,0,0;1.5708rad)
FEATURE [Part::Feature] Shape002  label="C12_C_1206_3216Metric_613218D6"
  Placement = pos=(162.319,-113.02,-1.6) rot=(0,1,0;3.14159rad)
  shape: bbox 3.2 x 1.6 x 1.6 mm, 28 faces (baked)
FEATURE [App::Link] SW1_SW_Cherry_MX_PCB_cp_61322BA2_2__ln_001  label="SW21_SW_Cherry_MX_PCB_cp_61322899[2]"
  LinkPlacement = pos=(94.6997,-46.5508,0) rot=(0,0,1;0rad)
  LinkedObject = -> Shape
  Placement = pos=(94.6997,-46.5508,0) rot=(0,0,1;0rad)
FEATURE [App::Link] SW1_Keycap_adjusted_v39_61322BA2_3__ln_001  label="SW21_Keycap_adjusted v39_61322899[3]"
  LinkPlacement = pos=(94.6997,-46.5508,9) rot=(1,0,0;1.5708rad)
  LinkedObject = -> Shape001
  Placement = pos=(94.6997,-46.5508,9) rot=(1,0,0;1.5708rad)
FEATURE [App::Link] SW1_SW_Cherry_MX_PCB_cp_61322BA2_2__ln_002  label="SW45_SW_Cherry_MX_PCB_cp_6132284E[2]"
  LinkPlacement = pos=(186.108,-86.5558,0) rot=(0,0,1;0rad)
  LinkedObject = -> Shape
  Placement = pos=(186.108,-86.5558,0) rot=(0,0,1;0rad)
FEATURE [App::Link] SW1_Keycap_adjusted_v39_61322BA2_3__ln_002  label="SW45_Keycap_adjusted v39_6132284E[3]"
  LinkPlacement = pos=(186.108,-86.5558,9) rot=(1,0,0;1.5708rad)
  LinkedObject = -> Shape001
  Placement = pos=(186.108,-86.5558,9) rot=(1,0,0;1.5708rad)
FEATURE [App::Link] SW1_SW_Cherry_MX_PCB_cp_61322BA2_2__ln_003  label="SW43_SW_Cherry_MX_PCB_cp_61322791[2]"
  LinkPlacement = pos=(186.102,-48.4494,0) rot=(0,0,1;0rad)
  LinkedObject = -> Shape
  Placement = pos=(186.102,-48.4494,0) rot=(0,0,1;0rad)
FEATURE [App::Link] SW1_Keycap_adjusted_v39_61322BA2_3__ln_003  label="SW43_Keycap_adjusted v39_61322791[3]"
  LinkPlacement = pos=(186.102,-48.4494,9) rot=(1,0,0;1.5708rad)
  LinkedObject = -> Shape001
  Placement = pos=(186.102,-48.4494,9) rot=(1,0,0;1.5708rad)
FEATURE [App::Link] SW1_SW_Cherry_MX_PCB_cp_61322BA2_2__ln_004  label="SW26_SW_Cherry_MX_PCB_cp_613224C7[2]"
  LinkPlacement = pos=(113.756,-48.4494,0) rot=(0,0,1;0rad)
  LinkedObject = -> Shape
  Placement = pos=(113.756,-48.4494,0) rot=(0,0,1;0rad)
FEATURE [App::Link] SW1_Keycap_adjusted_v39_61322BA2_3__ln_004  label="SW26_Keycap_adjusted v39_613224C7[3]"
  LinkPlacement = pos=(113.756,-48.4494,9) rot=(1,0,0;1.5708rad)
  LinkedObject = -> Shape001
  Placement = pos=(113.756,-48.4494,9) rot=(1,0,0;1.5708rad)
FEATURE [App::Link] SW1_SW_Cherry_MX_PCB_cp_61322BA2_2__ln_005  label="SW16_SW_Cherry_MX_PCB_cp_61322539[2]"
  LinkPlacement = pos=(75.6497,-43.6298,0) rot=(0,0,1;0rad)
  LinkedObject = -> Shape
  Placement = pos=(75.6497,-43.6298,0) rot=(0,0,1;0rad)
FEATURE [App::Link] SW1_Keycap_adjusted_v39_61322BA2_3__ln_005  label="SW16_Keycap_adjusted v39_61322539[3]"
  LinkPlacement = pos=(75.6497,-43.6298,9) rot=(1,0,0;1.5708rad)
  LinkedObject = -> Shape001
  Placement = pos=(75.6497,-43.6298,9) rot=(1,0,0;1.5708rad)
FEATURE [App::Link] SW1_SW_Cherry_MX_PCB_cp_61322BA2_2__ln_006  label="SW72_SW_Cherry_MX_PCB_cp_61322746[2]"
  LinkPlacement = pos=(286.184,-126.307,0) rot=(0,0,1;0rad)
  LinkedObject = -> Shape
  Placement = pos=(286.184,-126.307,0) rot=(0,0,1;0rad)
FEATURE [App::Link] SW1_Keycap_adjusted_v39_61322BA2_3__ln_006  label="SW72_Keycap_adjusted v39_61322746[3]"
  LinkPlacement = pos=(286.184,-126.307,9) rot=(1,0,0;1.5708rad)
  LinkedObject = -> Shape001
  Placement = pos=(286.184,-126.307,9) rot=(1,0,0;1.5708rad)
FEATURE [App::Link] SW1_SW_Cherry_MX_PCB_cp_61322BA2_2__ln_007  label="SW71_SW_Cherry_MX_PCB_cp_6132247C[2]"
  LinkPlacement = pos=(286.184,-107.257,0) rot=(0,0,1;0rad)
  LinkedObject = -> Shape
  Placement = pos=(286.184,-107.257,0) rot=(0,0,1;0rad)
FEATURE [App::Link] SW1_Keycap_adjusted_v39_61322BA2_3__ln_007  label="SW71_Keycap_adjusted v39_6132247C[3]"
  LinkPlacement = pos=(286.184,-107.257,9) rot=(1,0,0;1.5708rad)
  LinkedObject = -> Shape001
  Placement = pos=(286.184,-107.257,9) rot=(1,0,0;1.5708rad)
FEATURE [App::Link] SW1_SW_Cherry_MX_PCB_cp_61322BA2_2__ln_008  label="SW70_SW_Cherry_MX_PCB_cp_61322665[2]"
  LinkPlacement = pos=(286.184,-88.2067,0) rot=(0,0,1;0rad)
  LinkedObject = -> Shape
  Placement = pos=(286.184,-88.2067,0) rot=(0,0,1;0rad)
FEATURE [App::Link] SW1_Keycap_adjusted_v39_61322BA2_3__ln_008  label="SW70_Keycap_adjusted v39_61322665[3]"
  LinkPlacement = pos=(286.184,-88.2067,9) rot=(1,0,0;1.5708rad)
  LinkedObject = -> Shape001
  Placement = pos=(286.184,-88.2067,9) rot=(1,0,0;1.5708rad)
FEATURE [App::Link] SW1_SW_Cherry_MX_PCB_cp_61322BA2_2__ln_009  label="SW69_SW_Cherry_MX_PCB_cp_6132261A[2]"
  LinkPlacement = pos=(286.184,-69.1568,0) rot=(0,0,1;0rad)
  LinkedObject = -> Shape
  Placement = pos=(286.184,-69.1568,0) rot=(0,0,1;0rad)
FEATURE [App::Link] SW1_Keycap_adjusted_v39_61322BA2_3__ln_009  label="SW69_Keycap_adjusted v39_6132261A[3]"
  LinkPlacement = pos=(286.184,-69.1568,9) rot=(1,0,0;1.5708rad)
  LinkedObject = -> Shape001
  Placement = pos=(286.184,-69.1568,9) rot=(1,0,0;1.5708rad)
FEATURE [App::Link] SW1_SW_Cherry_MX_PCB_cp_61322BA2_2__ln_010  label="SW68_SW_Cherry_MX_PCB_cp_613225CF[2]"
  LinkPlacement = pos=(286.184,-50.1067,0) rot=(0,0,1;0rad)
  LinkedObject = -> Shape
  Placement = pos=(286.184,-50.1067,0) rot=(0,0,1;0rad)
FEATURE [App::Link] SW1_Keycap_adjusted_v39_61322BA2_3__ln_010  label="SW68_Keycap_adjusted v39_613225CF[3]"
  LinkPlacement = pos=(286.184,-50.1067,9) rot=(1,0,0;1.5708rad)
  LinkedObject = -> Shape001
  Placement = pos=(286.184,-50.1067,9) rot=(1,0,0;1.5708rad)
FEATURE [App::Link] SW1_SW_Cherry_MX_PCB_cp_61322BA2_2__ln_011  label="SW67_SW_Cherry_MX_PCB_cp_61322584[2]"
  LinkPlacement = pos=(262.308,-126.307,0) rot=(0,0,1;0rad)
  LinkedObject = -> Shape
  Placement = pos=(262.308,-126.307,0) rot=(0,0,1;0rad)
FEATURE [App::Link] SW1_Keycap_adjusted_v39_61322BA2_3__ln_011  label="SW67_Keycap_adjusted v39_61322584[3]"
  LinkPlacement = pos=(262.308,-126.307,9) rot=(1,0,0;1.5708rad)
  LinkedObject = -> Shape001
  Placement = pos=(262.308,-126.307,9) rot=(1,0,0;1.5708rad)
FEATURE [App::Link] SW1_SW_Cherry_MX_PCB_cp_61322BA2_2__ln_012  label="SW66_SW_Cherry_MX_PCB_cp_613226FB[2]"
  LinkPlacement = pos=(262.308,-107.257,0) rot=(0,0,1;0rad)
  LinkedObject = -> Shape
  Placement = pos=(262.308,-107.257,0) rot=(0,0,1;0rad)
FEATURE [App::Link] SW1_Keycap_adjusted_v39_61322BA2_3__ln_012  label="SW66_Keycap_adjusted v39_613226FB[3]"
  LinkPlacement = pos=(262.308,-107.257,9) rot=(1,0,0;1.5708rad)
  LinkedObject = -> Shape001
  Placement = pos=(262.308,-107.257,9) rot=(1,0,0;1.5708rad)
FEATURE [App::Link] SW1_SW_Cherry_MX_PCB_cp_61322BA2_2__ln_013  label="SW65_SW_Cherry_MX_PCB_cp_61322803[2]"
  LinkPlacement = pos=(262.308,-88.2067,0) rot=(0,0,1;0rad)
  LinkedObject = -> Shape
  Placement = pos=(262.308,-88.2067,0) rot=(0,0,1;0rad)
FEATURE [App::Link] SW1_Keycap_adjusted_v39_61322BA2_3__ln_013  label="SW65_Keycap_adjusted v39_61322803[3]"
  LinkPlacement = pos=(262.308,-88.2067,9) rot=(1,0,0;1.5708rad)
  LinkedObject = -> Shape001
  Placement = pos=(262.308,-88.2067,9) rot=(1,0,0;1.5708rad)
FEATURE [App::Link] SW1_SW_Cherry_MX_PCB_cp_61322BA2_2__ln_014  label="SW64_SW_Cherry_MX_PCB_cp_613226B0[2]"
  LinkPlacement = pos=(262.308,-69.1568,0) rot=(0,0,1;0rad)
  LinkedObject = -> Shape
  Placement = pos=(262.308,-69.1568,0) rot=(0,0,1;0rad)
FEATURE [App::Link] SW1_Keycap_adjusted_v39_61322BA2_3__ln_014  label="SW64_Keycap_adjusted v39_613226B0[3]"
  LinkPlacement = pos=(262.308,-69.1568,9) rot=(1,0,0;1.5708rad)
  LinkedObject = -> Shape001
  Placement = pos=(262.308,-69.1568,9) rot=(1,0,0;1.5708rad)
FEATURE [App::Link] SW1_SW_Cherry_MX_PCB_cp_61322BA2_2__ln_015  label="SW63_SW_Cherry_MX_PCB_cp_61322143[2]"
  LinkPlacement = pos=(262.308,-50.1067,0) rot=(0,0,1;0rad)
  LinkedObject = -> Shape
  Placement = pos=(262.308,-50.1067,0) rot=(0,0,1;0rad)
FEATURE [App::Link] SW1_Keycap_adjusted_v39_61322BA2_3__ln_015  label="SW63_Keycap_adjusted v39_61322143[3]"
  LinkPlacement = pos=(262.308,-50.1067,9) rot=(1,0,0;1.5708rad)
  LinkedObject = -> Shape001
  Placement = pos=(262.308,-50.1067,9) rot=(1,0,0;1.5708rad)
FEATURE [App::Link] SW1_SW_Cherry_MX_PCB_cp_61322BA2_2__ln_016  label="SW62_SW_Cherry_MX_PCB_cp_61322062[2]"
  LinkPlacement = pos=(243.258,-122.751,0) rot=(0,0,1;0rad)
  LinkedObject = -> Shape
  Placement = pos=(243.258,-122.751,0) rot=(0,0,1;0rad)
FEATURE [App::Link] SW1_Keycap_adjusted_v39_61322BA2_3__ln_016  label="SW62_Keycap_adjusted v39_61322062[3]"
  LinkPlacement = pos=(243.258,-122.751,9) rot=(1,0,0;1.5708rad)
  LinkedObject = -> Shape001
  Placement = pos=(243.258,-122.751,9) rot=(1,0,0;1.5708rad)
FEATURE [App::Link] SW1_SW_Cherry_MX_PCB_cp_61322BA2_2__ln_017  label="SW61_SW_Cherry_MX_PCB_cp_613220F8[2]"
  LinkPlacement = pos=(243.258,-103.701,0) rot=(0,0,1;0rad)
  LinkedObject = -> Shape
  Placement = pos=(243.258,-103.701,0) rot=(0,0,1;0rad)
FEATURE [App::Link] SW1_Keycap_adjusted_v39_61322BA2_3__ln_017  label="SW61_Keycap_adjusted v39_613220F8[3]"
  LinkPlacement = pos=(243.258,-103.701,9) rot=(1,0,0;1.5708rad)
  LinkedObject = -> Shape001
  Placement = pos=(243.258,-103.701,9) rot=(1,0,0;1.5708rad)
FEATURE [App::Link] SW1_SW_Cherry_MX_PCB_cp_61322BA2_2__ln_018  label="SW60_SW_Cherry_MX_PCB_cp_613220AD[2]"
  LinkPlacement = pos=(243.258,-84.6508,0) rot=(0,0,1;0rad)
  LinkedObject = -> Shape
  Placement = pos=(243.258,-84.6508,0) rot=(0,0,1;0rad)
FEATURE [App::Link] SW1_Keycap_adjusted_v39_61322BA2_3__ln_018  label="SW60_Keycap_adjusted v39_613220AD[3]"
  LinkPlacement = pos=(243.258,-84.6508,9) rot=(1,0,0;1.5708rad)
  LinkedObject = -> Shape001
  Placement = pos=(243.258,-84.6508,9) rot=(1,0,0;1.5708rad)
FEATURE [App::Link] SW1_SW_Cherry_MX_PCB_cp_61322BA2_2__ln_019  label="SW59_SW_Cherry_MX_PCB_cp_6132218E[2]"
  LinkPlacement = pos=(243.258,-65.6008,0) rot=(0,0,1;0rad)
  LinkedObject = -> Shape
  Placement = pos=(243.258,-65.6008,0) rot=(0,0,1;0rad)
FEATURE [App::Link] SW1_Keycap_adjusted_v39_61322BA2_3__ln_019  label="SW59_Keycap_adjusted v39_6132218E[3]"
  LinkPlacement = pos=(243.258,-65.6008,9) rot=(1,0,0;1.5708rad)
  LinkedObject = -> Shape001
  Placement = pos=(243.258,-65.6008,9) rot=(1,0,0;1.5708rad)
FEATURE [App::Link] SW1_SW_Cherry_MX_PCB_cp_61322BA2_2__ln_020  label="SW58_SW_Cherry_MX_PCB_cp_6132226F[2]"
  LinkPlacement = pos=(243.258,-46.5508,0) rot=(0,0,1;0rad)
  LinkedObject = -> Shape
  Placement = pos=(243.258,-46.5508,0) rot=(0,0,1;0rad)
FEATURE [App::Link] SW1_Keycap_adjusted_v39_61322BA2_3__ln_020  label="SW58_Keycap_adjusted v39_6132226F[3]"
  LinkPlacement = pos=(243.258,-46.5508,9) rot=(1,0,0;1.5708rad)
  LinkedObject = -> Shape001
  Placement = pos=(243.258,-46.5508,9) rot=(1,0,0;1.5708rad)
FEATURE [App::Link] SW1_SW_Cherry_MX_PCB_cp_61322BA2_2__ln_021  label="SW57_SW_Cherry_MX_PCB_cp_61322431[2]"
  LinkPlacement = pos=(224.208,-119.83,0) rot=(0,0,1;0rad)
  LinkedObject = -> Shape
  Placement = pos=(224.208,-119.83,0) rot=(0,0,1;0rad)
FEATURE [App::Link] SW1_Keycap_adjusted_v39_61322BA2_3__ln_021  label="SW57_Keycap_adjusted v39_61322431[3]"
  LinkPlacement = pos=(224.208,-119.83,9) rot=(1,0,0;1.5708rad)
  LinkedObject = -> Shape001
  Placement = pos=(224.208,-119.83,9) rot=(1,0,0;1.5708rad)
FEATURE [App::Link] SW1_SW_Cherry_MX_PCB_cp_61322BA2_2__ln_022  label="SW56_SW_Cherry_MX_PCB_cp_61321FCC[2]"
  LinkPlacement = pos=(224.208,-100.78,0) rot=(0,0,1;0rad)
  LinkedObject = -> Shape
  Placement = pos=(224.208,-100.78,0) rot=(0,0,1;0rad)
FEATURE [App::Link] SW1_Keycap_adjusted_v39_61322BA2_3__ln_022  label="SW56_Keycap_adjusted v39_61321FCC[3]"
  LinkPlacement = pos=(224.208,-100.78,9) rot=(1,0,0;1.5708rad)
  LinkedObject = -> Shape001
  Placement = pos=(224.208,-100.78,9) rot=(1,0,0;1.5708rad)
FEATURE [App::Link] SW1_SW_Cherry_MX_PCB_cp_61322BA2_2__ln_023  label="SW55_SW_Cherry_MX_PCB_cp_61321F81[2]"
  LinkPlacement = pos=(224.208,-81.7297,0) rot=(0,0,1;0rad)
  LinkedObject = -> Shape
  Placement = pos=(224.208,-81.7297,0) rot=(0,0,1;0rad)
FEATURE [App::Link] SW1_Keycap_adjusted_v39_61322BA2_3__ln_023  label="SW55_Keycap_adjusted v39_61321F81[3]"
  LinkPlacement = pos=(224.208,-81.7297,9) rot=(1,0,0;1.5708rad)
  LinkedObject = -> Shape001
  Placement = pos=(224.208,-81.7297,9) rot=(1,0,0;1.5708rad)
FEATURE [App::Link] SW1_SW_Cherry_MX_PCB_cp_61322BA2_2__ln_024  label="SW54_SW_Cherry_MX_PCB_cp_61322350[2]"
  LinkPlacement = pos=(224.208,-62.6797,0) rot=(0,0,1;0rad)
  LinkedObject = -> Shape
  Placement = pos=(224.208,-62.6797,0) rot=(0,0,1;0rad)
FEATURE [App::Link] SW1_Keycap_adjusted_v39_61322BA2_3__ln_024  label="SW54_Keycap_adjusted v39_61322350[3]"
  LinkPlacement = pos=(224.208,-62.6797,9) rot=(1,0,0;1.5708rad)
  LinkedObject = -> Shape001
  Placement = pos=(224.208,-62.6797,9) rot=(1,0,0;1.5708rad)
FEATURE [App::Link] SW1_SW_Cherry_MX_PCB_cp_61322BA2_2__ln_025  label="SW53_SW_Cherry_MX_PCB_cp_61321F36[2]"
  LinkPlacement = pos=(224.208,-43.6298,0) rot=(0,0,1;0rad)
  LinkedObject = -> Shape
  Placement = pos=(224.208,-43.6298,0) rot=(0,0,1;0rad)
FEATURE [App::Link] SW1_Keycap_adjusted_v39_61322BA2_3__ln_025  label="SW53_Keycap_adjusted v39_61321F36[3]"
  LinkPlacement = pos=(224.208,-43.6298,9) rot=(1,0,0;1.5708rad)
  LinkedObject = -> Shape001
  Placement = pos=(224.208,-43.6298,9) rot=(1,0,0;1.5708rad)
FEATURE [App::Link] SW1_SW_Cherry_MX_PCB_cp_61322BA2_2__ln_026  label="SW52_SW_Cherry_MX_PCB_cp_61322305[2]"
  LinkPlacement = pos=(205.158,-122.751,0) rot=(0,0,1;0rad)
  LinkedObject = -> Shape
  Placement = pos=(205.158,-122.751,0) rot=(0,0,1;0rad)
FEATURE [App::Link] SW1_Keycap_adjusted_v39_61322BA2_3__ln_026  label="SW52_Keycap_adjusted v39_61322305[3]"
  LinkPlacement = pos=(205.158,-122.751,9) rot=(1,0,0;1.5708rad)
  LinkedObject = -> Shape001
  Placement = pos=(205.158,-122.751,9) rot=(1,0,0;1.5708rad)
FEATURE [App::Link] SW1_SW_Cherry_MX_PCB_cp_61322BA2_2__ln_027  label="SW51_SW_Cherry_MX_PCB_cp_613221D9[2]"
  LinkPlacement = pos=(205.158,-103.701,0) rot=(0,0,1;0rad)
  LinkedObject = -> Shape
  Placement = pos=(205.158,-103.701,0) rot=(0,0,1;0rad)
FEATURE [App::Link] SW1_Keycap_adjusted_v39_61322BA2_3__ln_027  label="SW51_Keycap_adjusted v39_613221D9[3]"
  LinkPlacement = pos=(205.158,-103.701,9) rot=(1,0,0;1.5708rad)
  LinkedObject = -> Shape001
  Placement = pos=(205.158,-103.701,9) rot=(1,0,0;1.5708rad)
FEATURE [App::Link] SW1_SW_Cherry_MX_PCB_cp_61322BA2_2__ln_028  label="SW50_SW_Cherry_MX_PCB_cp_3223000000.0[2]"
  LinkPlacement = pos=(205.158,-84.6508,0) rot=(0,0,1;0rad)
  LinkedObject = -> Shape
  Placement = pos=(205.158,-84.6508,0) rot=(0,0,1;0rad)
FEATURE [App::Link] SW1_Keycap_adjusted_v39_61322BA2_3__ln_028  label="SW50_Keycap_adjusted v39_3223000000.0[3]"
  LinkPlacement = pos=(205.158,-84.6508,9) rot=(1,0,0;1.5708rad)
  LinkedObject = -> Shape001
  Placement = pos=(205.158,-84.6508,9) rot=(1,0,0;1.5708rad)
FEATURE [App::Link] SW1_SW_Cherry_MX_PCB_cp_61322BA2_2__ln_029  label="SW49_SW_Cherry_MX_PCB_cp_61322224[2]"
  LinkPlacement = pos=(205.158,-65.6008,0) rot=(0,0,1;0rad)
  LinkedObject = -> Shape
  Placement = pos=(205.158,-65.6008,0) rot=(0,0,1;0rad)
FEATURE [App::Link] SW1_Keycap_adjusted_v39_61322BA2_3__ln_029  label="SW49_Keycap_adjusted v39_61322224[3]"
  LinkPlacement = pos=(205.158,-65.6008,9) rot=(1,0,0;1.5708rad)
  LinkedObject = -> Shape001
  Placement = pos=(205.158,-65.6008,9) rot=(1,0,0;1.5708rad)
FEATURE [App::Link] SW1_SW_Cherry_MX_PCB_cp_61322BA2_2__ln_030  label="SW48_SW_Cherry_MX_PCB_cp_6132239B[2]"
  LinkPlacement = pos=(205.158,-46.5508,0) rot=(0,0,1;0rad)
  LinkedObject = -> Shape
  Placement = pos=(205.158,-46.5508,0) rot=(0,0,1;0rad)
FEATURE [App::Link] SW1_Keycap_adjusted_v39_61322BA2_3__ln_030  label="SW48_Keycap_adjusted v39_6132239B[3]"
  LinkPlacement = pos=(205.158,-46.5508,9) rot=(1,0,0;1.5708rad)
  LinkedObject = -> Shape001
  Placement = pos=(205.158,-46.5508,9) rot=(1,0,0;1.5708rad)
FEATURE [App::Link] SW1_SW_Cherry_MX_PCB_cp_61322BA2_2__ln_031  label="SW47_SW_Cherry_MX_PCB_cp_61322017[2]"
  LinkPlacement = pos=(182.507,-128.157,0) rot=(0,0,1;0.523599rad)
  LinkedObject = -> Shape
  Placement = pos=(182.507,-128.157,0) rot=(0,0,1;0.523599rad)
FEATURE [App::Link] SW1_Keycap_adjusted_v39_61322BA2_3__ln_031  label="SW47_Keycap_adjusted v39_61322017[3]"
  LinkPlacement = pos=(182.507,-128.157,9) rot=(0.935113,0.250563,0.250563;1.63783rad)
  LinkedObject = -> Shape001
  Placement = pos=(182.507,-128.157,9) rot=(0.935113,0.250563,0.250563;1.63783rad)
FEATURE [App::Link] SW1_SW_Cherry_MX_PCB_cp_61322BA2_2__ln_032  label="SW46_SW_Cherry_MX_PCB_cp_613222BA[2]"
  LinkPlacement = pos=(186.108,-105.606,0) rot=(0,0,1;0rad)
  LinkedObject = -> Shape
  Placement = pos=(186.108,-105.606,0) rot=(0,0,1;0rad)
FEATURE [App::Link] SW1_Keycap_adjusted_v39_61322BA2_3__ln_032  label="SW46_Keycap_adjusted v39_613222BA[3]"
  LinkPlacement = pos=(186.108,-105.606,9) rot=(1,0,0;1.5708rad)
  LinkedObject = -> Shape001
  Placement = pos=(186.108,-105.606,9) rot=(1,0,0;1.5708rad)
FEATURE [App::Link] SW1_SW_Cherry_MX_PCB_cp_61322BA2_2__ln_033  label="SW44_SW_Cherry_MX_PCB_cp_613219DB[2]"
  LinkPlacement = pos=(186.108,-67.5058,0) rot=(0,0,1;0rad)
  LinkedObject = -> Shape
  Placement = pos=(186.108,-67.5058,0) rot=(0,0,1;0rad)
FEATURE [App::Link] SW1_Keycap_adjusted_v39_61322BA2_3__ln_033  label="SW44_Keycap_adjusted v39_613219DB[3]"
  LinkPlacement = pos=(186.108,-67.5058,9) rot=(1,0,0;1.5708rad)
  LinkedObject = -> Shape001
  Placement = pos=(186.108,-67.5058,9) rot=(1,0,0;1.5708rad)
FEATURE [App::Link] SW1_SW_Cherry_MX_PCB_cp_61322BA2_2__ln_034  label="SW42_SW_Cherry_MX_PCB_cp_61321990[2]"
  LinkPlacement = pos=(165.466,-141.161,0) rot=(0,0,1;0.785398rad)
  LinkedObject = -> Shape
  Placement = pos=(165.466,-141.161,0) rot=(0,0,1;0.785398rad)
FEATURE [App::Link] SW1_Keycap_adjusted_v39_61322BA2_3__ln_034  label="SW42_Keycap_adjusted v39_61321990[3]"
  LinkPlacement = pos=(165.466,-141.161,9) rot=(0.862856,0.357407,0.357407;1.71777rad)
  LinkedObject = -> Shape001
  Placement = pos=(165.466,-141.161,9) rot=(0.862856,0.357407,0.357407;1.71777rad)
FEATURE [App::Link] SW1_SW_Cherry_MX_PCB_cp_61322BA2_2__ln_035  label="SW41_SW_Cherry_MX_PCB_cp_61321945[2]"
  LinkPlacement = pos=(167.058,-107.257,0) rot=(0,0,1;0rad)
  LinkedObject = -> Shape
  Placement = pos=(167.058,-107.257,0) rot=(0,0,1;0rad)
FEATURE [App::Link] SW1_Keycap_adjusted_v39_61322BA2_3__ln_035  label="SW41_Keycap_adjusted v39_61321945[3]"
  LinkPlacement = pos=(167.058,-107.257,9) rot=(1,0,0;1.5708rad)
  LinkedObject = -> Shape001
  Placement = pos=(167.058,-107.257,9) rot=(1,0,0;1.5708rad)
FEATURE [App::Link] SW1_SW_Cherry_MX_PCB_cp_61322BA2_2__ln_036  label="SW40_SW_Cherry_MX_PCB_cp_6132431B[2]"
  LinkPlacement = pos=(167.058,-88.2067,0) rot=(0,0,1;0rad)
  LinkedObject = -> Shape
  Placement = pos=(167.058,-88.2067,0) rot=(0,0,1;0rad)
FEATURE [App::Link] SW1_Keycap_adjusted_v39_61322BA2_3__ln_036  label="SW40_Keycap_adjusted v39_6132431B[3]"
  LinkPlacement = pos=(167.058,-88.2067,9) rot=(1,0,0;1.5708rad)
  LinkedObject = -> Shape001
  Placement = pos=(167.058,-88.2067,9) rot=(1,0,0;1.5708rad)
FEATURE [App::Link] SW1_SW_Cherry_MX_PCB_cp_61322BA2_2__ln_037  label="SW39_SW_Cherry_MX_PCB_cp_61321BE8[2]"
  LinkPlacement = pos=(167.058,-69.1568,0) rot=(0,0,1;0rad)
  LinkedObject = -> Shape
  Placement = pos=(167.058,-69.1568,0) rot=(0,0,1;0rad)
FEATURE [App::Link] SW1_Keycap_adjusted_v39_61322BA2_3__ln_037  label="SW39_Keycap_adjusted v39_61321BE8[3]"
  LinkPlacement = pos=(167.058,-69.1568,9) rot=(1,0,0;1.5708rad)
  LinkedObject = -> Shape001
  Placement = pos=(167.058,-69.1568,9) rot=(1,0,0;1.5708rad)
FEATURE [App::Link] SW1_SW_Cherry_MX_PCB_cp_61322BA2_2__ln_038  label="SW38_SW_Cherry_MX_PCB_cp_61321A71[2]"
  LinkPlacement = pos=(167.058,-50.1067,0) rot=(0,0,1;0rad)
  LinkedObject = -> Shape
  Placement = pos=(167.058,-50.1067,0) rot=(0,0,1;0rad)
FEATURE [App::Link] SW1_Keycap_adjusted_v39_61322BA2_3__ln_038  label="SW38_Keycap_adjusted v39_61321A71[3]"
  LinkPlacement = pos=(167.058,-50.1067,9) rot=(1,0,0;1.5708rad)
  LinkedObject = -> Shape001
  Placement = pos=(167.058,-50.1067,9) rot=(1,0,0;1.5708rad)
FEATURE [Part::Feature] Shape003  label="D68_D_1206_61321C2C"
  Placement = pos=(295.796,-85.7467,0) rot=(0,0,1;3.14159rad)
  shape: bbox 3.4 x 1.87 x 0.96 mm, 39 faces (baked)
FEATURE [App::Link] D68_D_1206_61321C2C_ln_  label="D60_D_1206_6.1321e+37"
  LinkPlacement = pos=(252.74,-120.291,0) rot=(0,0,1;3.14159rad)
  LinkedObject = -> Shape003
  Placement = pos=(252.74,-120.291,0) rot=(0,0,1;3.14159rad)
FEATURE [App::Link] D68_D_1206_61321C2C_ln_001  label="D45_D_1206_61321908"
  LinkPlacement = pos=(189.682,-121.245,0) rot=(0,0,1;3.66519rad)
  LinkedObject = -> Shape003
  Placement = pos=(189.682,-121.245,0) rot=(0,0,1;3.66519rad)
FEATURE [Part::Feature] Shape004  label="U2_TQFP_44_10x10mm_P08mm_6.1321e+103"
  Placement = pos=(196.196,-74.92,-1.6) rot=(0.92388,0.382683,0;3.14159rad)
  shape: bbox 14.39 x 14.39 x 1.1 mm, 704 faces (baked)
FEATURE [App::Link] U2_TQFP_44_10x10mm_P08mm_6_1321e_103_ln_  label="U1_TQFP_44_10x10mm_P08mm_61321C92"
  LinkPlacement = pos=(104.852,-75.428,-1.6) rot=(0.92388,0.382683,0;3.14159rad)
  LinkedObject = -> Shape004
  Placement = pos=(104.852,-75.428,-1.6) rot=(0.92388,0.382683,0;3.14159rad)
FEATURE [App::Link] SW1_SW_Cherry_MX_PCB_cp_61322BA2_2__ln_039  label="SW35_SW_Cherry_MX_PCB_cp_61321B9D[2]"
  LinkPlacement = pos=(134.314,-141.236,0) rot=(0,0,-1;0.785398rad)
  LinkedObject = -> Shape
  Placement = pos=(134.314,-141.236,0) rot=(0,0,-1;0.785398rad)
FEATURE [App::Link] SW1_Keycap_adjusted_v39_61322BA2_3__ln_039  label="SW35_Keycap_adjusted v39_61321B9D[3]"
  LinkPlacement = pos=(134.314,-141.236,9) rot=(0.862856,-0.357407,-0.357407;1.71777rad)
  LinkedObject = -> Shape001
  Placement = pos=(134.314,-141.236,9) rot=(0.862856,-0.357407,-0.357407;1.71777rad)
FEATURE [App::Link] SW1_SW_Cherry_MX_PCB_cp_61322BA2_2__ln_040  label="SW34_SW_Cherry_MX_PCB_cp_61321B07[2]"
  LinkPlacement = pos=(132.8,-107.257,0) rot=(0,0,1;0rad)
  LinkedObject = -> Shape
  Placement = pos=(132.8,-107.257,0) rot=(0,0,1;0rad)
FEATURE [App::Link] SW1_Keycap_adjusted_v39_61322BA2_3__ln_040  label="SW34_Keycap_adjusted v39_61321B07[3]"
  LinkPlacement = pos=(132.8,-107.257,9) rot=(1,0,0;1.5708rad)
  LinkedObject = -> Shape001
  Placement = pos=(132.8,-107.257,9) rot=(1,0,0;1.5708rad)
FEATURE [App::Link] SW1_SW_Cherry_MX_PCB_cp_61322BA2_2__ln_041  label="SW33_SW_Cherry_MX_PCB_cp_61321D2F[2]"
  LinkPlacement = pos=(132.8,-88.2067,0) rot=(0,0,1;0rad)
  LinkedObject = -> Shape
  Placement = pos=(132.8,-88.2067,0) rot=(0,0,1;0rad)
FEATURE [App::Link] SW1_Keycap_adjusted_v39_61322BA2_3__ln_041  label="SW33_Keycap_adjusted v39_61321D2F[3]"
  LinkPlacement = pos=(132.8,-88.2067,9) rot=(1,0,0;1.5708rad)
  LinkedObject = -> Shape001
  Placement = pos=(132.8,-88.2067,9) rot=(1,0,0;1.5708rad)
FEATURE [App::Link] SW1_SW_Cherry_MX_PCB_cp_61322BA2_2__ln_042  label="SW32_SW_Cherry_MX_PCB_cp_61321B52[2]"
  LinkPlacement = pos=(132.8,-69.1568,0) rot=(0,0,1;0rad)
  LinkedObject = -> Shape
  Placement = pos=(132.8,-69.1568,0) rot=(0,0,1;0rad)
FEATURE [App::Link] SW1_Keycap_adjusted_v39_61322BA2_3__ln_042  label="SW32_Keycap_adjusted v39_61321B52[3]"
  LinkPlacement = pos=(132.8,-69.1568,9) rot=(1,0,0;1.5708rad)
  LinkedObject = -> Shape001
  Placement = pos=(132.8,-69.1568,9) rot=(1,0,0;1.5708rad)
FEATURE [App::Link] SW1_SW_Cherry_MX_PCB_cp_61322BA2_2__ln_043  label="SW31_SW_Cherry_MX_PCB_cp_61321ABC[2]"
  LinkPlacement = pos=(132.8,-50.1067,0) rot=(0,0,1;0rad)
  LinkedObject = -> Shape
  Placement = pos=(132.8,-50.1067,0) rot=(0,0,1;0rad)
FEATURE [App::Link] SW1_Keycap_adjusted_v39_61322BA2_3__ln_043  label="SW31_Keycap_adjusted v39_61321ABC[3]"
  LinkPlacement = pos=(132.8,-50.1067,9) rot=(1,0,0;1.5708rad)
  LinkedObject = -> Shape001
  Placement = pos=(132.8,-50.1067,9) rot=(1,0,0;1.5708rad)
FEATURE [App::Link] SW1_SW_Cherry_MX_PCB_cp_61322BA2_2__ln_044  label="SW30_SW_Cherry_MX_PCB_cp_61321A26[2]"
  LinkPlacement = pos=(117.34,-128.242,0) rot=(0,0,-1;0.523599rad)
  LinkedObject = -> Shape
  Placement = pos=(117.34,-128.242,0) rot=(0,0,-1;0.523599rad)
FEATURE [App::Link] SW1_Keycap_adjusted_v39_61322BA2_3__ln_044  label="SW30_Keycap_adjusted v39_61321A26[3]"
  LinkPlacement = pos=(117.34,-128.242,9) rot=(0.935113,-0.250563,-0.250563;1.63783rad)
  LinkedObject = -> Shape001
  Placement = pos=(117.34,-128.242,9) rot=(0.935113,-0.250563,-0.250563;1.63783rad)
FEATURE [App::Link] SW1_SW_Cherry_MX_PCB_cp_61322BA2_2__ln_045  label="SW29_SW_Cherry_MX_PCB_cp_613213EA[2]"
  LinkPlacement = pos=(113.75,-105.606,0) rot=(0,0,1;0rad)
  LinkedObject = -> Shape
  Placement = pos=(113.75,-105.606,0) rot=(0,0,1;0rad)
FEATURE [App::Link] SW1_Keycap_adjusted_v39_61322BA2_3__ln_045  label="SW29_Keycap_adjusted v39_613213EA[3]"
  LinkPlacement = pos=(113.75,-105.606,9) rot=(1,0,0;1.5708rad)
  LinkedObject = -> Shape001
  Placement = pos=(113.75,-105.606,9) rot=(1,0,0;1.5708rad)
FEATURE [App::Link] SW1_SW_Cherry_MX_PCB_cp_61322BA2_2__ln_046  label="SW28_SW_Cherry_MX_PCB_cp_61321354[2]"
  LinkPlacement = pos=(113.75,-86.5558,0) rot=(0,0,1;0rad)
  LinkedObject = -> Shape
  Placement = pos=(113.75,-86.5558,0) rot=(0,0,1;0rad)
FEATURE [App::Link] SW1_Keycap_adjusted_v39_61322BA2_3__ln_046  label="SW28_Keycap_adjusted v39_61321354[3]"
  LinkPlacement = pos=(113.75,-86.5558,9) rot=(1,0,0;1.5708rad)
  LinkedObject = -> Shape001
  Placement = pos=(113.75,-86.5558,9) rot=(1,0,0;1.5708rad)
FEATURE [App::Link] SW1_SW_Cherry_MX_PCB_cp_61322BA2_2__ln_047  label="SW27_SW_Cherry_MX_PCB_cp_6132139F[2]"
  LinkPlacement = pos=(113.75,-67.5058,0) rot=(0,0,1;0rad)
  LinkedObject = -> Shape
  Placement = pos=(113.75,-67.5058,0) rot=(0,0,1;0rad)
FEATURE [App::Link] SW1_Keycap_adjusted_v39_61322BA2_3__ln_047  label="SW27_Keycap_adjusted v39_6132139F[3]"
  LinkPlacement = pos=(113.75,-67.5058,9) rot=(1,0,0;1.5708rad)
  LinkedObject = -> Shape001
  Placement = pos=(113.75,-67.5058,9) rot=(1,0,0;1.5708rad)
FEATURE [App::Link] SW1_SW_Cherry_MX_PCB_cp_61322BA2_2__ln_048  label="SW25_SW_Cherry_MX_PCB_cp_61321480[2]"
  LinkPlacement = pos=(94.6997,-122.751,0) rot=(0,0,1;0rad)
  LinkedObject = -> Shape
  Placement = pos=(94.6997,-122.751,0) rot=(0,0,1;0rad)
FEATURE [App::Link] SW1_Keycap_adjusted_v39_61322BA2_3__ln_048  label="SW25_Keycap_adjusted v39_61321480[3]"
  LinkPlacement = pos=(94.6997,-122.751,9) rot=(1,0,0;1.5708rad)
  LinkedObject = -> Shape001
  Placement = pos=(94.6997,-122.751,9) rot=(1,0,0;1.5708rad)
FEATURE [App::Link] SW1_SW_Cherry_MX_PCB_cp_61322BA2_2__ln_049  label="SW24_SW_Cherry_MX_PCB_cp_613215F7[2]"
  LinkPlacement = pos=(94.6997,-103.701,0) rot=(0,0,1;0rad)
  LinkedObject = -> Shape
  Placement = pos=(94.6997,-103.701,0) rot=(0,0,1;0rad)
FEATURE [App::Link] SW1_Keycap_adjusted_v39_61322BA2_3__ln_049  label="SW24_Keycap_adjusted v39_613215F7[3]"
  LinkPlacement = pos=(94.6997,-103.701,9) rot=(1,0,0;1.5708rad)
  LinkedObject = -> Shape001
  Placement = pos=(94.6997,-103.701,9) rot=(1,0,0;1.5708rad)
FEATURE [App::Link] SW1_SW_Cherry_MX_PCB_cp_61322BA2_2__ln_050  label="SW23_SW_Cherry_MX_PCB_cp_61321435[2]"
  LinkPlacement = pos=(94.6997,-84.6508,0) rot=(0,0,1;0rad)
  LinkedObject = -> Shape
  Placement = pos=(94.6997,-84.6508,0) rot=(0,0,1;0rad)
FEATURE [App::Link] SW1_Keycap_adjusted_v39_61322BA2_3__ln_050  label="SW23_Keycap_adjusted v39_61321435[3]"
  LinkPlacement = pos=(94.6997,-84.6508,9) rot=(1,0,0;1.5708rad)
  LinkedObject = -> Shape001
  Placement = pos=(94.6997,-84.6508,9) rot=(1,0,0;1.5708rad)
FEATURE [App::Link] SW1_SW_Cherry_MX_PCB_cp_61322BA2_2__ln_051  label="SW22_SW_Cherry_MX_PCB_cp_613215AC[2]"
  LinkPlacement = pos=(94.6997,-65.6008,0) rot=(0,0,1;0rad)
  LinkedObject = -> Shape
  Placement = pos=(94.6997,-65.6008,0) rot=(0,0,1;0rad)
FEATURE [App::Link] SW1_Keycap_adjusted_v39_61322BA2_3__ln_051  label="SW22_Keycap_adjusted v39_613215AC[3]"
  LinkPlacement = pos=(94.6997,-65.6008,9) rot=(1,0,0;1.5708rad)
  LinkedObject = -> Shape001
  Placement = pos=(94.6997,-65.6008,9) rot=(1,0,0;1.5708rad)
FEATURE [App::Link] SW1_SW_Cherry_MX_PCB_cp_61322BA2_2__ln_052  label="SW20_SW_Cherry_MX_PCB_cp_613212BE[2]"
  LinkPlacement = pos=(75.6497,-119.83,0) rot=(0,0,1;0rad)
  LinkedObject = -> Shape
  Placement = pos=(75.6497,-119.83,0) rot=(0,0,1;0rad)
FEATURE [App::Link] SW1_Keycap_adjusted_v39_61322BA2_3__ln_052  label="SW20_Keycap_adjusted v39_613212BE[3]"
  LinkPlacement = pos=(75.6497,-119.83,9) rot=(1,0,0;1.5708rad)
  LinkedObject = -> Shape001
  Placement = pos=(75.6497,-119.83,9) rot=(1,0,0;1.5708rad)
FEATURE [App::Link] SW1_SW_Cherry_MX_PCB_cp_61322BA2_2__ln_053  label="SW19_SW_Cherry_MX_PCB_cp_61321273[2]"
  LinkPlacement = pos=(75.6497,-100.78,0) rot=(0,0,1;0rad)
  LinkedObject = -> Shape
  Placement = pos=(75.6497,-100.78,0) rot=(0,0,1;0rad)
FEATURE [App::Link] SW1_Keycap_adjusted_v39_61322BA2_3__ln_053  label="SW19_Keycap_adjusted v39_61321273[3]"
  LinkPlacement = pos=(75.6497,-100.78,9) rot=(1,0,0;1.5708rad)
  LinkedObject = -> Shape001
  Placement = pos=(75.6497,-100.78,9) rot=(1,0,0;1.5708rad)
FEATURE [App::Link] SW1_SW_Cherry_MX_PCB_cp_61322BA2_2__ln_054  label="SW18_SW_Cherry_MX_PCB_cp_61321192[2]"
  LinkPlacement = pos=(75.6497,-81.7297,0) rot=(0,0,1;0rad)
  LinkedObject = -> Shape
  Placement = pos=(75.6497,-81.7297,0) rot=(0,0,1;0rad)
FEATURE [App::Link] SW1_Keycap_adjusted_v39_61322BA2_3__ln_054  label="SW18_Keycap_adjusted v39_61321192[3]"
  LinkPlacement = pos=(75.6497,-81.7297,9) rot=(1,0,0;1.5708rad)
  LinkedObject = -> Shape001
  Placement = pos=(75.6497,-81.7297,9) rot=(1,0,0;1.5708rad)
FEATURE [App::Link] SW1_SW_Cherry_MX_PCB_cp_61322BA2_2__ln_055  label="SW17_SW_Cherry_MX_PCB_cp_61321309[2]"
  LinkPlacement = pos=(75.6497,-62.6797,0) rot=(0,0,1;0rad)
  LinkedObject = -> Shape
  Placement = pos=(75.6497,-62.6797,0) rot=(0,0,1;0rad)
FEATURE [App::Link] SW1_Keycap_adjusted_v39_61322BA2_3__ln_055  label="SW17_Keycap_adjusted v39_61321309[3]"
  LinkPlacement = pos=(75.6497,-62.6797,9) rot=(1,0,0;1.5708rad)
  LinkedObject = -> Shape001
  Placement = pos=(75.6497,-62.6797,9) rot=(1,0,0;1.5708rad)
FEATURE [App::Link] SW1_SW_Cherry_MX_PCB_cp_61322BA2_2__ln_056  label="SW15_SW_Cherry_MX_PCB_cp_613211DD[2]"
  LinkPlacement = pos=(56.5998,-122.751,0) rot=(0,0,1;0rad)
  LinkedObject = -> Shape
  Placement = pos=(56.5998,-122.751,0) rot=(0,0,1;0rad)
FEATURE [App::Link] SW1_Keycap_adjusted_v39_61322BA2_3__ln_056  label="SW15_Keycap_adjusted v39_613211DD[3]"
  LinkPlacement = pos=(56.5998,-122.751,9) rot=(1,0,0;1.5708rad)
  LinkedObject = -> Shape001
  Placement = pos=(56.5998,-122.751,9) rot=(1,0,0;1.5708rad)
FEATURE [App::Link] SW1_SW_Cherry_MX_PCB_cp_61322BA2_2__ln_057  label="SW14_SW_Cherry_MX_PCB_cp_6132168D[2]"
  LinkPlacement = pos=(56.5998,-103.701,0) rot=(0,0,1;0rad)
  LinkedObject = -> Shape
  Placement = pos=(56.5998,-103.701,0) rot=(0,0,1;0rad)
FEATURE [App::Link] SW1_Keycap_adjusted_v39_61322BA2_3__ln_057  label="SW14_Keycap_adjusted v39_6132168D[3]"
  LinkPlacement = pos=(56.5998,-103.701,9) rot=(1,0,0;1.5708rad)
  LinkedObject = -> Shape001
  Placement = pos=(56.5998,-103.701,9) rot=(1,0,0;1.5708rad)
FEATURE [App::Link] SW1_SW_Cherry_MX_PCB_cp_61322BA2_2__ln_058  label="SW13_SW_Cherry_MX_PCB_cp_61321642[2]"
  LinkPlacement = pos=(56.5998,-84.6508,0) rot=(0,0,1;0rad)
  LinkedObject = -> Shape
  Placement = pos=(56.5998,-84.6508,0) rot=(0,0,1;0rad)
FEATURE [App::Link] SW1_Keycap_adjusted_v39_61322BA2_3__ln_058  label="SW13_Keycap_adjusted v39_61321642[3]"
  LinkPlacement = pos=(56.5998,-84.6508,9) rot=(1,0,0;1.5708rad)
  LinkedObject = -> Shape001
  Placement = pos=(56.5998,-84.6508,9) rot=(1,0,0;1.5708rad)
FEATURE [App::Link] SW1_SW_Cherry_MX_PCB_cp_61322BA2_2__ln_059  label="SW12_SW_Cherry_MX_PCB_cp_61321561[2]"
  LinkPlacement = pos=(56.5998,-65.6008,0) rot=(0,0,1;0rad)
  LinkedObject = -> Shape
  Placement = pos=(56.5998,-65.6008,0) rot=(0,0,1;0rad)
FEATURE [App::Link] SW1_Keycap_adjusted_v39_61322BA2_3__ln_059  label="SW12_Keycap_adjusted v39_61321561[3]"
  LinkPlacement = pos=(56.5998,-65.6008,9) rot=(1,0,0;1.5708rad)
  LinkedObject = -> Shape001
  Placement = pos=(56.5998,-65.6008,9) rot=(1,0,0;1.5708rad)
FEATURE [App::Link] SW1_SW_Cherry_MX_PCB_cp_61322BA2_2__ln_060  label="SW11_SW_Cherry_MX_PCB_cp_61321228[2]"
  LinkPlacement = pos=(56.5998,-46.5508,0) rot=(0,0,1;0rad)
  LinkedObject = -> Shape
  Placement = pos=(56.5998,-46.5508,0) rot=(0,0,1;0rad)
FEATURE [App::Link] SW1_Keycap_adjusted_v39_61322BA2_3__ln_060  label="SW11_Keycap_adjusted v39_61321228[3]"
  LinkPlacement = pos=(56.5998,-46.5508,9) rot=(1,0,0;1.5708rad)
  LinkedObject = -> Shape001
  Placement = pos=(56.5998,-46.5508,9) rot=(1,0,0;1.5708rad)
FEATURE [App::Link] SW1_SW_Cherry_MX_PCB_cp_61322BA2_2__ln_061  label="SW10_SW_Cherry_MX_PCB_cp_61321516[2]"
  LinkPlacement = pos=(37.5498,-126.307,0) rot=(0,0,1;0rad)
  LinkedObject = -> Shape
  Placement = pos=(37.5498,-126.307,0) rot=(0,0,1;0rad)
FEATURE [App::Link] SW1_Keycap_adjusted_v39_61322BA2_3__ln_061  label="SW10_Keycap_adjusted v39_61321516[3]"
  LinkPlacement = pos=(37.5498,-126.307,9) rot=(1,0,0;1.5708rad)
  LinkedObject = -> Shape001
  Placement = pos=(37.5498,-126.307,9) rot=(1,0,0;1.5708rad)
FEATURE [App::Link] SW1_SW_Cherry_MX_PCB_cp_61322BA2_2__ln_062  label="SW9_SW_Cherry_MX_PCB_cp_613214CB[2]"
  LinkPlacement = pos=(37.5498,-107.257,0) rot=(0,0,1;0rad)
  LinkedObject = -> Shape
  Placement = pos=(37.5498,-107.257,0) rot=(0,0,1;0rad)
FEATURE [App::Link] SW1_Keycap_adjusted_v39_61322BA2_3__ln_062  label="SW9_Keycap_adjusted v39_613214CB[3]"
  LinkPlacement = pos=(37.5498,-107.257,9) rot=(1,0,0;1.5708rad)
  LinkedObject = -> Shape001
  Placement = pos=(37.5498,-107.257,9) rot=(1,0,0;1.5708rad)
FEATURE [App::Link] SW1_SW_Cherry_MX_PCB_cp_61322BA2_2__ln_063  label="SW8_SW_Cherry_MX_PCB_cp_61322F02[2]"
  LinkPlacement = pos=(37.5498,-88.2067,0) rot=(0,0,1;0rad)
  LinkedObject = -> Shape
  Placement = pos=(37.5498,-88.2067,0) rot=(0,0,1;0rad)
FEATURE [App::Link] SW1_Keycap_adjusted_v39_61322BA2_3__ln_063  label="SW8_Keycap_adjusted v39_61322F02[3]"
  LinkPlacement = pos=(37.5498,-88.2067,9) rot=(1,0,0;1.5708rad)
  LinkedObject = -> Shape001
  Placement = pos=(37.5498,-88.2067,9) rot=(1,0,0;1.5708rad)
FEATURE [App::Link] SW1_SW_Cherry_MX_PCB_cp_61322BA2_2__ln_064  label="SW7_SW_Cherry_MX_PCB_cp_61322F4D[2]"
  LinkPlacement = pos=(37.5498,-69.1568,0) rot=(0,0,1;0rad)
  LinkedObject = -> Shape
  Placement = pos=(37.5498,-69.1568,0) rot=(0,0,1;0rad)
FEATURE [App::Link] SW1_Keycap_adjusted_v39_61322BA2_3__ln_064  label="SW7_Keycap_adjusted v39_61322F4D[3]"
  LinkPlacement = pos=(37.5498,-69.1568,9) rot=(1,0,0;1.5708rad)
  LinkedObject = -> Shape001
  Placement = pos=(37.5498,-69.1568,9) rot=(1,0,0;1.5708rad)
FEATURE [App::Link] SW1_SW_Cherry_MX_PCB_cp_61322BA2_2__ln_065  label="SW6_SW_Cherry_MX_PCB_cp_61322B57[2]"
  LinkPlacement = pos=(37.5498,-50.1067,0) rot=(0,0,1;0rad)
  LinkedObject = -> Shape
  Placement = pos=(37.5498,-50.1067,0) rot=(0,0,1;0rad)
FEATURE [App::Link] SW1_Keycap_adjusted_v39_61322BA2_3__ln_065  label="SW6_Keycap_adjusted v39_61322B57[3]"
  LinkPlacement = pos=(37.5498,-50.1067,9) rot=(1,0,0;1.5708rad)
  LinkedObject = -> Shape001
  Placement = pos=(37.5498,-50.1067,9) rot=(1,0,0;1.5708rad)
FEATURE [App::Link] SW1_SW_Cherry_MX_PCB_cp_61322BA2_2__ln_066  label="SW5_SW_Cherry_MX_PCB_cp_61322C83[2]"
  LinkPlacement = pos=(13.6737,-126.307,0) rot=(0,0,1;0rad)
  LinkedObject = -> Shape
  Placement = pos=(13.6737,-126.307,0) rot=(0,0,1;0rad)
FEATURE [App::Link] SW1_Keycap_adjusted_v39_61322BA2_3__ln_066  label="SW5_Keycap_adjusted v39_61322C83[3]"
  LinkPlacement = pos=(13.6737,-126.307,9) rot=(1,0,0;1.5708rad)
  LinkedObject = -> Shape001
  Placement = pos=(13.6737,-126.307,9) rot=(1,0,0;1.5708rad)
FEATURE [App::Link] SW1_SW_Cherry_MX_PCB_cp_61322BA2_2__ln_067  label="SW4_SW_Cherry_MX_PCB_cp_61322C38[2]"
  LinkPlacement = pos=(13.6737,-107.257,0) rot=(0,0,1;0rad)
  LinkedObject = -> Shape
  Placement = pos=(13.6737,-107.257,0) rot=(0,0,1;0rad)
FEATURE [App::Link] SW1_Keycap_adjusted_v39_61322BA2_3__ln_067  label="SW4_Keycap_adjusted v39_61322C38[3]"
  LinkPlacement = pos=(13.6737,-107.257,9) rot=(1,0,0;1.5708rad)
  LinkedObject = -> Shape001
  Placement = pos=(13.6737,-107.257,9) rot=(1,0,0;1.5708rad)
FEATURE [App::Link] SW1_SW_Cherry_MX_PCB_cp_61322BA2_2__ln_068  label="SW3_SW_Cherry_MX_PCB_cp_61322BED[2]"
  LinkPlacement = pos=(13.6737,-88.2067,0) rot=(0,0,1;0rad)
  LinkedObject = -> Shape
  Placement = pos=(13.6737,-88.2067,0) rot=(0,0,1;0rad)
FEATURE [App::Link] SW1_Keycap_adjusted_v39_61322BA2_3__ln_068  label="SW3_Keycap_adjusted v39_61322BED[3]"
  LinkPlacement = pos=(13.6737,-88.2067,9) rot=(1,0,0;1.5708rad)
  LinkedObject = -> Shape001
  Placement = pos=(13.6737,-88.2067,9) rot=(1,0,0;1.5708rad)
FEATURE [Part::Feature] Shape005  label="R8_R_1206_3216Metric_6.1322e+19"
  Placement = pos=(131.363,-33.4862,-1.6) rot=(-0.707107,0.707107,0;3.14159rad)
  shape: bbox 1.6 x 3.2 x 0.55 mm, 26 faces (baked)
FEATURE [App::Link] R8_R_1206_3216Metric_6_1322e_19_ln_  label="R7_R_1206_3216Metric_61322D85"
  LinkPlacement = pos=(134.093,-33.4862,-1.6) rot=(-0.707107,0.707107,0;3.14159rad)
  LinkedObject = -> Shape005
  Placement = pos=(134.093,-33.4862,-1.6) rot=(-0.707107,0.707107,0;3.14159rad)
FEATURE [App::Link] R8_R_1206_3216Metric_6_1322e_19_ln_001  label="R6_R_1206_3216Metric_61322DB5"
  LinkPlacement = pos=(215.5,-72.38,-1.6) rot=(1,0,0;3.14159rad)
  LinkedObject = -> Shape005
  Placement = pos=(215.5,-72.38,-1.6) rot=(1,0,0;3.14159rad)
FEATURE [App::Link] R8_R_1206_3216Metric_6_1322e_19_ln_002  label="R5_R_1206_3216Metric_61322DE5"
  LinkPlacement = pos=(176.511,-55.997,-1.6) rot=(0.707107,0.707107,0;3.14159rad)
  LinkedObject = -> Shape005
  Placement = pos=(176.511,-55.997,-1.6) rot=(0.707107,0.707107,0;3.14159rad)
FEATURE [App::Link] R8_R_1206_3216Metric_6_1322e_19_ln_003  label="R4_R_1206_3216Metric_61322D55"
  LinkPlacement = pos=(124.028,-72.761,-1.6) rot=(-0.707107,0.707107,0;3.14159rad)
  LinkedObject = -> Shape005
  Placement = pos=(124.028,-72.761,-1.6) rot=(-0.707107,0.707107,0;3.14159rad)
FEATURE [App::Link] R8_R_1206_3216Metric_6_1322e_19_ln_004  label="R3_R_1206_3216Metric_61322D25"
  LinkPlacement = pos=(135.966,-74.031,-1.6) rot=(0,1,0;3.14159rad)
  LinkedObject = -> Shape005
  Placement = pos=(135.966,-74.031,-1.6) rot=(0,1,0;3.14159rad)
FEATURE [App::Link] R8_R_1206_3216Metric_6_1322e_19_ln_005  label="R2_R_1206_3216Metric_61322CF5"
  LinkPlacement = pos=(135.966,-77.46,-1.6) rot=(0,1,0;3.14159rad)
  LinkedObject = -> Shape005
  Placement = pos=(135.966,-77.46,-1.6) rot=(0,1,0;3.14159rad)
FEATURE [App::Link] R8_R_1206_3216Metric_6_1322e_19_ln_006  label="R1_R_1206_3216Metric_61322CC5"
  LinkPlacement = pos=(92.7865,-76.698,-1.6) rot=(0.707107,0.707107,0;3.14159rad)
  LinkedObject = -> Shape005
  Placement = pos=(92.7865,-76.698,-1.6) rot=(0.707107,0.707107,0;3.14159rad)
FEATURE [App::Link] D68_D_1206_61321C2C_ln_002  label="D70_D_1206_1323500000.0"
  LinkPlacement = pos=(295.796,-123.847,0) rot=(0,0,1;3.14159rad)
  LinkedObject = -> Shape003
  Placement = pos=(295.796,-123.847,0) rot=(0,0,1;3.14159rad)
FEATURE [App::Link] D68_D_1206_61321C2C_ln_003  label="D69_D_1206_613233FF"
  LinkPlacement = pos=(295.796,-104.797,0) rot=(0,0,1;3.14159rad)
  LinkedObject = -> Shape003
  Placement = pos=(295.796,-104.797,0) rot=(0,0,1;3.14159rad)
FEATURE [App::Link] D68_D_1206_61321C2C_ln_004  label="D67_D_1206_613235AF"
  LinkPlacement = pos=(295.796,-66.6967,0) rot=(0,0,1;3.14159rad)
  LinkedObject = -> Shape003
  Placement = pos=(295.796,-66.6967,0) rot=(0,0,1;3.14159rad)
FEATURE [App::Link] D68_D_1206_61321C2C_ln_005  label="D66_D_1206_6132335D"
  LinkPlacement = pos=(295.796,-48.631,0) rot=(0,0,1;3.14159rad)
  LinkedObject = -> Shape003
  Placement = pos=(295.796,-48.631,0) rot=(0,0,1;3.14159rad)
FEATURE [App::Link] D68_D_1206_61321C2C_ln_006  label="D65_D_1206_61323579"
  LinkPlacement = pos=(271.793,-123.847,0) rot=(0,0,1;3.14159rad)
  LinkedObject = -> Shape003
  Placement = pos=(271.793,-123.847,0) rot=(0,0,1;3.14159rad)
FEATURE [App::Link] D68_D_1206_61321C2C_ln_007  label="D64_D_1206_61323651"
  LinkPlacement = pos=(271.793,-104.797,0) rot=(0,0,1;3.14159rad)
  LinkedObject = -> Shape003
  Placement = pos=(271.793,-104.797,0) rot=(0,0,1;3.14159rad)
FEATURE [App::Link] D68_D_1206_61321C2C_ln_008  label="D63_D_1206_6132361B"
  LinkPlacement = pos=(271.79,-85.7468,0) rot=(0,0,1;3.14159rad)
  LinkedObject = -> Shape003
  Placement = pos=(271.79,-85.7468,0) rot=(0,0,1;3.14159rad)
FEATURE [App::Link] D68_D_1206_61321C2C_ln_009  label="D62_D_1206_613234D7"
  LinkPlacement = pos=(271.793,-66.6967,0) rot=(0,0,1;3.14159rad)
  LinkedObject = -> Shape003
  Placement = pos=(271.793,-66.6967,0) rot=(0,0,1;3.14159rad)
FEATURE [App::Link] D68_D_1206_61321C2C_ln_010  label="D61_D_1206_613233C9"
  LinkPlacement = pos=(271.793,-47.6467,0) rot=(0,0,1;3.14159rad)
  LinkedObject = -> Shape003
  Placement = pos=(271.793,-47.6467,0) rot=(0,0,1;3.14159rad)
FEATURE [App::Link] D68_D_1206_61321C2C_ln_011  label="D59_D_1206_61323543"
  LinkPlacement = pos=(252.743,-101.241,0) rot=(0,0,1;3.14159rad)
  LinkedObject = -> Shape003
  Placement = pos=(252.743,-101.241,0) rot=(0,0,1;3.14159rad)
FEATURE [App::Link] D68_D_1206_61321C2C_ln_012  label="D58_D_1206_613236F3"
  LinkPlacement = pos=(252.743,-82.1907,0) rot=(0,0,1;3.14159rad)
  LinkedObject = -> Shape003
  Placement = pos=(252.743,-82.1907,0) rot=(0,0,1;3.14159rad)
FEATURE [App::Link] D68_D_1206_61321C2C_ln_013  label="D57_D_1206_613236BD"
  LinkPlacement = pos=(252.743,-63.1407,0) rot=(0,0,1;3.14159rad)
  LinkedObject = -> Shape003
  Placement = pos=(252.743,-63.1407,0) rot=(0,0,1;3.14159rad)
FEATURE [App::Link] D68_D_1206_61321C2C_ln_014  label="D56_D_1206_6132350D"
  LinkPlacement = pos=(252.743,-44.0907,0) rot=(0,0,1;3.14159rad)
  LinkedObject = -> Shape003
  Placement = pos=(252.743,-44.0907,0) rot=(0,0,1;3.14159rad)
FEATURE [App::Link] D68_D_1206_61321C2C_ln_015  label="D55_D_1206_61323687"
  LinkPlacement = pos=(233.693,-117.37,0) rot=(0,0,1;3.14159rad)
  LinkedObject = -> Shape003
  Placement = pos=(233.693,-117.37,0) rot=(0,0,1;3.14159rad)
FEATURE [App::Link] D68_D_1206_61321C2C_ln_016  label="D54_D_1206_613234A1"
  LinkPlacement = pos=(233.693,-98.3197,0) rot=(0,0,1;3.14159rad)
  LinkedObject = -> Shape003
  Placement = pos=(233.693,-98.3197,0) rot=(0,0,1;3.14159rad)
FEATURE [App::Link] D68_D_1206_61321C2C_ln_017  label="D53_D_1206_6132346B"
  LinkPlacement = pos=(233.754,-79.2698,0) rot=(0,0,1;3.14159rad)
  LinkedObject = -> Shape003
  Placement = pos=(233.754,-79.2698,0) rot=(0,0,1;3.14159rad)
FEATURE [App::Link] D68_D_1206_61321C2C_ln_018  label="D52_D_1206_61323435"
  LinkPlacement = pos=(233.693,-60.2197,0) rot=(0,0,1;3.14159rad)
  LinkedObject = -> Shape003
  Placement = pos=(233.693,-60.2197,0) rot=(0,0,1;3.14159rad)
FEATURE [App::Link] D68_D_1206_61321C2C_ln_019  label="D51_D_1206_61323393"
  LinkPlacement = pos=(233.69,-41.1698,0) rot=(0,0,1;3.14159rad)
  LinkedObject = -> Shape003
  Placement = pos=(233.69,-41.1698,0) rot=(0,0,1;3.14159rad)
FEATURE [App::Link] D68_D_1206_61321C2C_ln_020  label="D50_D_1206_61323033"
  LinkPlacement = pos=(214.643,-120.291,0) rot=(0,0,1;3.14159rad)
  LinkedObject = -> Shape003
  Placement = pos=(214.643,-120.291,0) rot=(0,0,1;3.14159rad)
FEATURE [App::Link] D68_D_1206_61321C2C_ln_021  label="D49_D_1206_61322FFD"
  LinkPlacement = pos=(214.643,-101.241,0) rot=(0,0,1;3.14159rad)
  LinkedObject = -> Shape003
  Placement = pos=(214.643,-101.241,0) rot=(0,0,1;3.14159rad)
FEATURE [App::Link] D68_D_1206_61321C2C_ln_022  label="D48_D_1206_613231000.0"
  LinkPlacement = pos=(214.643,-82.1907,0) rot=(0,0,1;3.14159rad)
  LinkedObject = -> Shape003
  Placement = pos=(214.643,-82.1907,0) rot=(0,0,1;3.14159rad)
FEATURE [App::Link] D68_D_1206_61321C2C_ln_023  label="D47_D_1206_61323285"
  LinkPlacement = pos=(214.707,-63.1407,0) rot=(0,0,1;3.14159rad)
  LinkedObject = -> Shape003
  Placement = pos=(214.707,-63.1407,0) rot=(0,0,1;3.14159rad)
FEATURE [App::Link] D68_D_1206_61321C2C_ln_024  label="D46_D_1206_61323069"
  LinkPlacement = pos=(214.643,-44.0907,0) rot=(0,0,1;3.14159rad)
  LinkedObject = -> Shape003
  Placement = pos=(214.643,-44.0907,0) rot=(0,0,1;3.14159rad)
FEATURE [App::Link] D68_D_1206_61321C2C_ln_025  label="D44_D_1206_613231AD"
  LinkPlacement = pos=(195.593,-103.146,0) rot=(0,0,1;3.14159rad)
  LinkedObject = -> Shape003
  Placement = pos=(195.593,-103.146,0) rot=(0,0,1;3.14159rad)
FEATURE [App::Link] D68_D_1206_61321C2C_ln_026  label="D43_D_1206_61323327"
  LinkPlacement = pos=(195.593,-84.0957,0) rot=(0,0,1;3.14159rad)
  LinkedObject = -> Shape003
  Placement = pos=(195.593,-84.0957,0) rot=(0,0,1;3.14159rad)
FEATURE [App::Link] D68_D_1206_61321C2C_ln_027  label="D42_D_1206_613232F1"
  LinkPlacement = pos=(195.593,-65.0457,0) rot=(0,0,1;3.14159rad)
  LinkedObject = -> Shape003
  Placement = pos=(195.593,-65.0457,0) rot=(0,0,1;3.14159rad)
FEATURE [App::Link] D68_D_1206_61321C2C_ln_028  label="D41_D_1206_613232BB"
  LinkPlacement = pos=(195.593,-45.9958,0) rot=(0,0,1;3.14159rad)
  LinkedObject = -> Shape003
  Placement = pos=(195.593,-45.9958,0) rot=(0,0,1;3.14159rad)
FEATURE [App::Link] D68_D_1206_61321C2C_ln_029  label="D40_D_1206_61323141"
  LinkPlacement = pos=(170.447,-132.737,0) rot=(0,0,1;3.92699rad)
  LinkedObject = -> Shape003
  Placement = pos=(170.447,-132.737,0) rot=(0,0,1;3.92699rad)
FEATURE [App::Link] D68_D_1206_61321C2C_ln_030  label="D39_D_1206_613230D5"
  LinkPlacement = pos=(176.543,-104.797,0) rot=(0,0,1;3.14159rad)
  LinkedObject = -> Shape003
  Placement = pos=(176.543,-104.797,0) rot=(0,0,1;3.14159rad)
FEATURE [App::Link] D68_D_1206_61321C2C_ln_031  label="D38_D_1206_61323177"
  LinkPlacement = pos=(176.543,-85.7468,0) rot=(0,0,1;3.14159rad)
  LinkedObject = -> Shape003
  Placement = pos=(176.543,-85.7468,0) rot=(0,0,1;3.14159rad)
FEATURE [App::Link] D68_D_1206_61321C2C_ln_032  label="D37_D_1206_6132324F"
  LinkPlacement = pos=(176.543,-66.6967,0) rot=(0,0,1;3.14159rad)
  LinkedObject = -> Shape003
  Placement = pos=(176.543,-66.6967,0) rot=(0,0,1;3.14159rad)
FEATURE [App::Link] D68_D_1206_61321C2C_ln_033  label="D36_D_1206_61323219"
  LinkPlacement = pos=(176.543,-47.6468,0) rot=(0,0,1;3.14159rad)
  LinkedObject = -> Shape003
  Placement = pos=(176.543,-47.6468,0) rot=(0,0,1;3.14159rad)
FEATURE [App::Link] D68_D_1206_61321C2C_ln_034  label="D35_D_1206_6132309F"
  LinkPlacement = pos=(129.458,-132.737,0) rot=(0,0,-1;0.785398rad)
  LinkedObject = -> Shape003
  Placement = pos=(129.458,-132.737,0) rot=(0,0,-1;0.785398rad)
FEATURE [App::Link] D68_D_1206_61321C2C_ln_035  label="D34_D_1206_6132310B"
  LinkPlacement = pos=(123.235,-104.797,0) rot=(0,0,1;0rad)
  LinkedObject = -> Shape003
  Placement = pos=(123.235,-104.797,0) rot=(0,0,1;0rad)
FEATURE [App::Link] D68_D_1206_61321C2C_ln_036  label="D33_D_1206_61322FC7"
  LinkPlacement = pos=(123.235,-85.7468,0) rot=(0,0,1;0rad)
  LinkedObject = -> Shape003
  Placement = pos=(123.235,-85.7468,0) rot=(0,0,1;0rad)
FEATURE [App::Link] D68_D_1206_61321C2C_ln_037  label="D32_D_1206_61322F91"
  LinkPlacement = pos=(123.235,-66.6967,0) rot=(0,0,1;0rad)
  LinkedObject = -> Shape003
  Placement = pos=(123.235,-66.6967,0) rot=(0,0,1;0rad)
FEATURE [App::Link] D68_D_1206_61321C2C_ln_038  label="D31_D_1206_61320FA5"
  LinkPlacement = pos=(123.235,-47.6467,0) rot=(0,0,1;0rad)
  LinkedObject = -> Shape003
  Placement = pos=(123.235,-47.6467,0) rot=(0,0,1;0rad)
FEATURE [App::Link] D68_D_1206_61321C2C_ln_039  label="D30_D_1206_61321155"
  LinkPlacement = pos=(110.281,-121.434,0) rot=(0,0,-1;0.523599rad)
  LinkedObject = -> Shape003
  Placement = pos=(110.281,-121.434,0) rot=(0,0,-1;0.523599rad)
FEATURE [App::Link] D68_D_1206_61321C2C_ln_040  label="D29_D_1206_61320D1D"
  LinkPlacement = pos=(104.185,-103.019,0) rot=(0,0,1;0rad)
  LinkedObject = -> Shape003
  Placement = pos=(104.185,-103.019,0) rot=(0,0,1;0rad)
FEATURE [App::Link] D68_D_1206_61321C2C_ln_041  label="D28_D_1206_61320E2B"
  LinkPlacement = pos=(104.185,-84.064,0) rot=(0,0,1;0rad)
  LinkedObject = -> Shape003
  Placement = pos=(104.185,-84.064,0) rot=(0,0,1;0rad)
FEATURE [App::Link] D68_D_1206_61321C2C_ln_042  label="D27_D_1206_61320F03"
  LinkPlacement = pos=(104.185,-65.0457,0) rot=(0,0,1;0rad)
  LinkedObject = -> Shape003
  Placement = pos=(104.185,-65.0457,0) rot=(0,0,1;0rad)
FEATURE [App::Link] D68_D_1206_61321C2C_ln_043  label="D26_D_1206_61320B8B"
  LinkPlacement = pos=(104.185,-45.9958,0) rot=(0,0,1;0rad)
  LinkedObject = -> Shape003
  Placement = pos=(104.185,-45.9958,0) rot=(0,0,1;0rad)
FEATURE [App::Link] D68_D_1206_61321C2C_ln_044  label="D25_D_1206_6132111F"
  LinkPlacement = pos=(85.1347,-120.291,0) rot=(0,0,1;0rad)
  LinkedObject = -> Shape003
  Placement = pos=(85.1347,-120.291,0) rot=(0,0,1;0rad)
FEATURE [App::Link] D68_D_1206_61321C2C_ln_045  label="D24_D_1206_61320B1F"
  LinkPlacement = pos=(85.1347,-101.241,0) rot=(0,0,1;0rad)
  LinkedObject = -> Shape003
  Placement = pos=(85.1347,-101.241,0) rot=(0,0,1;0rad)
FEATURE [App::Link] D68_D_1206_61321C2C_ln_046  label="D23_D_1206_61320AE9"
  LinkPlacement = pos=(85.1347,-82.0637,0) rot=(0,0,1;0rad)
  LinkedObject = -> Shape003
  Placement = pos=(85.1347,-82.0637,0) rot=(0,0,1;0rad)
FEATURE [App::Link] D68_D_1206_61321C2C_ln_047  label="D22_D_1206_61320ECD"
  LinkPlacement = pos=(85.1347,-63.1407,0) rot=(0,0,1;0rad)
  LinkedObject = -> Shape003
  Placement = pos=(85.1347,-63.1407,0) rot=(0,0,1;0rad)
FEATURE [App::Link] D68_D_1206_61321C2C_ln_048  label="D21_D_1206_0000000000.0"
  LinkPlacement = pos=(85.1347,-44.0907,0) rot=(0,0,1;0rad)
  LinkedObject = -> Shape003
  Placement = pos=(85.1347,-44.0907,0) rot=(0,0,1;0rad)
FEATURE [App::Link] D68_D_1206_61321C2C_ln_049  label="D20_D_1206_61320D53"
  LinkPlacement = pos=(66.0847,-117.497,0) rot=(0,0,1;0rad)
  LinkedObject = -> Shape003
  Placement = pos=(66.0847,-117.497,0) rot=(0,0,1;0rad)
FEATURE [App::Link] D68_D_1206_61321C2C_ln_050  label="D19_D_1206_61321011"
  LinkPlacement = pos=(66.0847,-98.4467,0) rot=(0,0,1;0rad)
  LinkedObject = -> Shape003
  Placement = pos=(66.0847,-98.4467,0) rot=(0,0,1;0rad)
FEATURE [App::Link] D68_D_1206_61321C2C_ln_051  label="D18_D_1206_61320B55"
  LinkPlacement = pos=(66.0847,-79.3967,0) rot=(0,0,1;0rad)
  LinkedObject = -> Shape003
  Placement = pos=(66.0847,-79.3967,0) rot=(0,0,1;0rad)
FEATURE [App::Link] D68_D_1206_61321C2C_ln_052  label="D17_D_1206_61320C81"
  LinkPlacement = pos=(66.0847,-60.3468,0) rot=(0,0,1;0rad)
  LinkedObject = -> Shape003
  Placement = pos=(66.0847,-60.3468,0) rot=(0,0,1;0rad)
FEATURE [App::Link] D68_D_1206_61321C2C_ln_053  label="D16_D_1206_61320F39"
  LinkPlacement = pos=(66.0847,-41.1698,0) rot=(0,0,1;0rad)
  LinkedObject = -> Shape003
  Placement = pos=(66.0847,-41.1698,0) rot=(0,0,1;0rad)
FEATURE [App::Link] D68_D_1206_61321C2C_ln_054  label="D15_D_1206_613210B3"
  LinkPlacement = pos=(47.0348,-120.291,0) rot=(0,0,1;0rad)
  LinkedObject = -> Shape003
  Placement = pos=(47.0348,-120.291,0) rot=(0,0,1;0rad)
FEATURE [App::Link] D68_D_1206_61321C2C_ln_055  label="D14_D_1206_61320A7D"
  LinkPlacement = pos=(47.0348,-101.241,0) rot=(0,0,1;0rad)
  LinkedObject = -> Shape003
  Placement = pos=(47.0348,-101.241,0) rot=(0,0,1;0rad)
FEATURE [App::Link] D68_D_1206_61321C2C_ln_056  label="D13_D_1206_61320AB3"
  LinkPlacement = pos=(47.0348,-82.1907,0) rot=(0,0,1;0rad)
  LinkedObject = -> Shape003
  Placement = pos=(47.0348,-82.1907,0) rot=(0,0,1;0rad)
FEATURE [App::Link] D68_D_1206_61321C2C_ln_057  label="D12_D_1206_61320A47"
  LinkPlacement = pos=(47.0318,-63.1407,0) rot=(0,0,1;0rad)
  LinkedObject = -> Shape003
  Placement = pos=(47.0318,-63.1407,0) rot=(0,0,1;0rad)
FEATURE [App::Link] D68_D_1206_61321C2C_ln_058  label="D11_D_1206_61320A11"
  LinkPlacement = pos=(47.0378,-44.0907,0) rot=(0,0,1;0rad)
  LinkedObject = -> Shape003
  Placement = pos=(47.0378,-44.0907,0) rot=(0,0,1;0rad)
FEATURE [App::Link] D68_D_1206_61321C2C_ln_059  label="D10_D_1206_6.132e+101"
  LinkPlacement = pos=(27.9847,-123.847,0) rot=(0,0,1;0rad)
  LinkedObject = -> Shape003
  Placement = pos=(27.9847,-123.847,0) rot=(0,0,1;0rad)
FEATURE [App::Link] D68_D_1206_61321C2C_ln_060  label="D9_D_1206_61320CB7"
  LinkPlacement = pos=(27.9847,-104.797,0) rot=(0,0,1;0rad)
  LinkedObject = -> Shape003
  Placement = pos=(27.9847,-104.797,0) rot=(0,0,1;0rad)
FEATURE [App::Link] D68_D_1206_61321C2C_ln_061  label="D8_D_1206_61320DF5"
  LinkPlacement = pos=(27.9847,-85.7468,0) rot=(0,0,1;0rad)
  LinkedObject = -> Shape003
  Placement = pos=(27.9847,-85.7468,0) rot=(0,0,1;0rad)
FEATURE [App::Link] D68_D_1206_61321C2C_ln_062  label="D7_D_1206_6132107D"
  LinkPlacement = pos=(27.9847,-66.6967,0) rot=(0,0,1;0rad)
  LinkedObject = -> Shape003
  Placement = pos=(27.9847,-66.6967,0) rot=(0,0,1;0rad)
FEATURE [App::Link] D68_D_1206_61321C2C_ln_063  label="D6_D_1206_61321047"
  LinkPlacement = pos=(27.9847,-47.6467,0) rot=(0,0,1;0rad)
  LinkedObject = -> Shape003
  Placement = pos=(27.9847,-47.6467,0) rot=(0,0,1;0rad)
FEATURE [App::Link] D68_D_1206_61321C2C_ln_064  label="D5_D_1206_61320FDB"
  LinkPlacement = pos=(4.10875,-123.847,0) rot=(0,0,1;0rad)
  LinkedObject = -> Shape003
  Placement = pos=(4.10875,-123.847,0) rot=(0,0,1;0rad)
FEATURE [App::Link] D68_D_1206_61321C2C_ln_065  label="D4_D_1206_61320F6F"
  LinkPlacement = pos=(4.10875,-104.797,0) rot=(0,0,1;0rad)
  LinkedObject = -> Shape003
  Placement = pos=(4.10875,-104.797,0) rot=(0,0,1;0rad)
FEATURE [App::Link] D68_D_1206_61321C2C_ln_066  label="D3_D_1206_6.132e+65"
  LinkPlacement = pos=(4.10875,-85.7468,0) rot=(0,0,1;0rad)
  LinkedObject = -> Shape003
  Placement = pos=(4.10875,-85.7468,0) rot=(0,0,1;0rad)
FEATURE [App::Link] D68_D_1206_61321C2C_ln_067  label="D2_D_1206_61320DBF"
  LinkPlacement = pos=(4.10875,-66.6967,0) rot=(0,0,1;0rad)
  LinkedObject = -> Shape003
  Placement = pos=(4.10875,-66.6967,0) rot=(0,0,1;0rad)
FEATURE [App::Link] D68_D_1206_61321C2C_ln_068  label="D1_D_1206_61320D89"
  LinkPlacement = pos=(4.10575,-49.4248,0) rot=(0,0,1;0rad)
  LinkedObject = -> Shape003
  Placement = pos=(4.10575,-49.4248,0) rot=(0,0,1;0rad)
FEATURE [App::Part] Top_2136
  Group = -> [Shape,Shape001,SW1_SW_Cherry_MX_PCB_cp_61322BA2_2__ln_,SW1_Keycap_adjusted_v39_61322BA2_3__ln_,SW1_SW_Cherry_MX_PCB_cp_61322BA2_2__ln_001,SW1_Keycap_adjusted_v39_61322BA2_3__ln_001,SW1_SW_Cherry_MX_PCB_cp_61322BA2_2__ln_002,SW1_Keycap_adjusted_v39_61322BA2_3__ln_002,SW1_SW_Cherry_MX_PCB_cp_61322BA2_2__ln_003,SW1_Keycap_adjusted_v39_61322BA2_3__ln_003,SW1_SW_Cherry_MX_PCB_cp_61322BA2_2__ln_004,+199 more]
  Origin = -> Origin003
FEATURE [App::Link] C12_C_1206_3216Metric_613218D6_ln_  label="C11_C_1206_3216Metric_61320CEB"
  LinkPlacement = pos=(176.511,-73.396,-1.6) rot=(1,0,0;3.14159rad)
  LinkedObject = -> Shape002
  Placement = pos=(176.511,-73.396,-1.6) rot=(1,0,0;3.14159rad)
FEATURE [App::Link] C12_C_1206_3216Metric_613218D6_ln_001  label="C10_C_1206_3216Metric_61320BBF"
  LinkPlacement = pos=(191.37,-56.759,-1.6) rot=(-0.707107,0.707107,0;3.14159rad)
  LinkedObject = -> Shape002
  Placement = pos=(191.37,-56.759,-1.6) rot=(-0.707107,0.707107,0;3.14159rad)
FEATURE [App::Link] C12_C_1206_3216Metric_613218D6_ln_002  label="C9_C_1206_3216Metric_61320C4F"
  LinkPlacement = pos=(198.355,-56.837,-1.6) rot=(0.707107,0.707107,0;3.14159rad)
  LinkedObject = -> Shape002
  Placement = pos=(198.355,-56.837,-1.6) rot=(0.707107,0.707107,0;3.14159rad)
FEATURE [App::Link] C12_C_1206_3216Metric_613218D6_ln_003  label="C8_C_1206_3216Metric_61320BEF"
  LinkPlacement = pos=(96.9775,-89.906,-1.6) rot=(0.92388,0.382683,0;3.14159rad)
  LinkedObject = -> Shape002
  Placement = pos=(96.9775,-89.906,-1.6) rot=(0.92388,0.382683,0;3.14159rad)
FEATURE [App::Link] C12_C_1206_3216Metric_613218D6_ln_004  label="C7_C_1206_3216Metric_61320C1F"
  LinkPlacement = pos=(86.9445,-77.587,-1.6) rot=(0,1,0;3.14159rad)
  LinkedObject = -> Shape002
  Placement = pos=(86.9445,-77.587,-1.6) rot=(0,1,0;3.14159rad)
FEATURE [App::Link] C12_C_1206_3216Metric_613218D6_ln_005  label="C6_C_1206_3216Metric_613208D4"
  LinkPlacement = pos=(86.9935,-70.856,-1.6) rot=(1,0,0;3.14159rad)
  LinkedObject = -> Shape002
  Placement = pos=(86.9935,-70.856,-1.6) rot=(1,0,0;3.14159rad)
FEATURE [App::Link] C12_C_1206_3216Metric_613218D6_ln_006  label="C5_C_1206_3216Metric_6132082F"
  LinkPlacement = pos=(137.363,-57.8385,-1.6) rot=(-0.707107,0.707107,0;3.14159rad)
  LinkedObject = -> Shape002
  Placement = pos=(137.363,-57.8385,-1.6) rot=(-0.707107,0.707107,0;3.14159rad)
FEATURE [App::Link] C12_C_1206_3216Metric_613218D6_ln_007  label="C4_C_1206_3216Metric_6132092B"
  LinkPlacement = pos=(134.442,-57.853,-1.6) rot=(-0.707107,0.707107,0;3.14159rad)
  LinkedObject = -> Shape002
  Placement = pos=(134.442,-57.853,-1.6) rot=(-0.707107,0.707107,0;3.14159rad)
FEATURE [App::Link] C12_C_1206_3216Metric_613218D6_ln_008  label="C3_C_1206_3216Metric_6132085F"
  LinkPlacement = pos=(131.712,-57.8385,-1.6) rot=(-0.707107,0.707107,0;3.14159rad)
  LinkedObject = -> Shape002
  Placement = pos=(131.712,-57.8385,-1.6) rot=(-0.707107,0.707107,0;3.14159rad)
FEATURE [App::Link] C12_C_1206_3216Metric_613218D6_ln_009  label="C2_C_1206_3216Metric_613207FF"
  LinkPlacement = pos=(128.95,-57.8385,-1.6) rot=(-0.707107,0.707107,0;3.14159rad)
  LinkedObject = -> Shape002
  Placement = pos=(128.95,-57.8385,-1.6) rot=(-0.707107,0.707107,0;3.14159rad)
FEATURE [App::Link] C12_C_1206_3216Metric_613218D6_ln_010  label="C1_C_1206_3216Metric_61320781"
  LinkPlacement = pos=(126.188,-57.853,-1.6) rot=(-0.707107,0.707107,0;3.14159rad)
  LinkedObject = -> Shape002
  Placement = pos=(126.188,-57.853,-1.6) rot=(-0.707107,0.707107,0;3.14159rad)
FEATURE [App::Part] Bot_2136
  Group = -> [Shape002,Shape004,U2_TQFP_44_10x10mm_P08mm_6_1321e_103_ln_,Shape005,R8_R_1206_3216Metric_6_1322e_19_ln_,R8_R_1206_3216Metric_6_1322e_19_ln_001,R8_R_1206_3216Metric_6_1322e_19_ln_002,R8_R_1206_3216Metric_6_1322e_19_ln_003,R8_R_1206_3216Metric_6_1322e_19_ln_004,R8_R_1206_3216Metric_6_1322e_19_ln_005,R8_R_1206_3216Metric_6_1322e_19_ln_006,C12_C_1206_3216Metric_613218D6_ln_,+10 more]
  Origin = -> Origin004
FEATURE [App::Part] Step_Models_2136
  Group = -> [Top_2136,Bot_2136]
  Origin = -> Origin002
FEATURE [App::Part] Board_2136  label="xenophon"
  Group = -> [Board_Geoms_2136,Step_Models_2136]
  Origin = -> Origin001
